FCSTD DOCUMENT  (FreeCAD 0.18R16146 (Git))
Label: ion
License: All rights reserved
LicenseURL: http://en.wikipedia.org/wiki/All_rights_reserved
objects: Part::Feature×332, Part::Part2DObjectPython×219, App::DocumentObjectGroup×23
note: 551 computed .brp shape members not serialized (recipe doc carries the construction recipe); baked Part::Feature solids carry a one-line shape summary decoded from their .brp

FEATURE [Part::Part2DObjectPython] Line030  # Draft 2D object (typed FeaturePython)
  ChamferSize = 0
  Closed = false
  End = (163,-79,0)
  FilletRadius = 0
  Length = 76
  MakeFace = false
  Placement = pos=(86,-79,0) rot=(0,0,1;0rad)
  Points = (2) [(1,0,0),(77,0,0)]
  Start = (87,-79,0)
  Subdivisions = 0
FEATURE [Part::Part2DObjectPython] Line038  # Draft 2D object (typed FeaturePython)
  ChamferSize = 0
  Closed = false
  End = (19.75,-79,0)
  FilletRadius = 0
  Length = 19.75
  MakeFace = false
  Placement = pos=(-4.8e-15,-79,0) rot=(0,0,1;0rad)
  Points = (2) [(4.8e-15,0,0),(19.75,0,0)]
  Start = (0,-79,0)
  Subdivisions = 0
FEATURE [Part::Part2DObjectPython] Arc  # Draft 2D object (typed FeaturePython)
  FirstAngle = 90
  LastAngle = 180
  MakeFace = false
  Placement = pos=(26.5,5,0) rot=(0,0,1;0rad)
  Radius = 1
FEATURE [Part::Part2DObjectPython] Arc001  # Draft 2D object (typed FeaturePython)
  FirstAngle = 0
  LastAngle = 90
  MakeFace = false
  Placement = pos=(32.5,5,0) rot=(0,0,1;0rad)
  Radius = 1
FEATURE [Part::Part2DObjectPython] Arc003  # Draft 2D object (typed FeaturePython)
  FirstAngle = -180
  LastAngle = -90
  MakeFace = false
  Placement = pos=(34.5,2,0) rot=(0,0,1;0rad)
  Radius = 1
FEATURE [Part::Part2DObjectPython] Line053  # Draft 2D object (typed FeaturePython)
  ChamferSize = 0
  Closed = false
  End = (25.5,2,0)
  FilletRadius = 0
  Length = 3
  MakeFace = false
  Placement = pos=(25.5,5,0) rot=(0,0,1;0rad)
  Points = (2) [(0,0,0),(0,-3,0)]
  Start = (25.5,5,0)
  Subdivisions = 0
FEATURE [Part::Part2DObjectPython] Line054  # Draft 2D object (typed FeaturePython)
  ChamferSize = 0
  Closed = true
  End = (32.5,6,0)
  FilletRadius = 0
  Length = 6
  MakeFace = false
  Placement = pos=(27,6,0) rot=(0,0,1;0rad)
  Points = (2) [(-0.5,-4.44089e-15,0),(5.5,-4.44089e-15,0)]
  Start = (26.5,6,0)
  Subdivisions = 0
FEATURE [Part::Part2DObjectPython] Line055  # Draft 2D object (typed FeaturePython)
  ChamferSize = 0
  Closed = false
  End = (33.5,2,0)
  FilletRadius = 0
  Length = 3
  MakeFace = false
  Placement = pos=(33.5,5,0) rot=(0,0,1;0rad)
  Points = (2) [(0,0,0),(0,-3,0)]
  Start = (33.5,5,0)
  Subdivisions = 0
FEATURE [Part::Part2DObjectPython] Arc004  # Draft 2D object (typed FeaturePython)
  FirstAngle = -90
  LastAngle = 0
  MakeFace = false
  Placement = pos=(81.75,2,0) rot=(0,0,1;0rad)
  Radius = 1
FEATURE [Part::Part2DObjectPython] Arc005  # Draft 2D object (typed FeaturePython)
  FirstAngle = -180
  LastAngle = -90
  MakeFace = false
  Placement = pos=(91.75,2,0) rot=(0,0,1;0rad)
  Radius = 1
FEATURE [Part::Part2DObjectPython] Line056  # Draft 2D object (typed FeaturePython)
  ChamferSize = 0
  Closed = false
  End = (90.75,2,0)
  FilletRadius = 0
  Length = 3
  MakeFace = false
  Placement = pos=(90.75,5,0) rot=(0,0,1;0rad)
  Points = (2) [(0,0,0),(0,-3,0)]
  Start = (90.75,5,0)
  Subdivisions = 0
FEATURE [Part::Part2DObjectPython] Arc006  # Draft 2D object (typed FeaturePython)
  FirstAngle = 0
  LastAngle = 90
  MakeFace = false
  Placement = pos=(89.75,5,0) rot=(0,0,1;0rad)
  Radius = 1
FEATURE [Part::Part2DObjectPython] Arc007  # Draft 2D object (typed FeaturePython)
  FirstAngle = 90
  LastAngle = 180
  MakeFace = false
  Placement = pos=(83.75,5,0) rot=(0,0,1;0rad)
  Radius = 1
FEATURE [Part::Part2DObjectPython] Line057  # Draft 2D object (typed FeaturePython)
  ChamferSize = 0
  Closed = false
  End = (82.75,2,0)
  FilletRadius = 0
  Length = 3
  MakeFace = false
  Placement = pos=(82.75,5,0) rot=(0,0,1;0rad)
  Points = (2) [(0,0,0),(0,-3,0)]
  Start = (82.75,5,0)
  Subdivisions = 0
FEATURE [Part::Part2DObjectPython] Line058  # Draft 2D object (typed FeaturePython)
  ChamferSize = 0
  Closed = false
  End = (89.75,6,0)
  FilletRadius = 0
  Length = 6
  MakeFace = false
  Placement = pos=(84.25,6,0) rot=(0,0,1;0rad)
  Points = (2) [(-0.5,-1.42109e-14,0),(5.5,-1.42109e-14,0)]
  Start = (83.75,6,0)
  Subdivisions = 0
FEATURE [App::DocumentObjectGroup] Group001  label="Nub2"
  Group = -> [Arc007,Arc006,Arc004,Arc005,Line057,Line058,Line056]
FEATURE [Part::Part2DObjectPython] Arc008  # Draft 2D object (typed FeaturePython)
  FirstAngle = -90
  LastAngle = 0
  MakeFace = false
  Placement = pos=(158.25,2,0) rot=(0,0,1;0rad)
  Radius = 1
FEATURE [Part::Part2DObjectPython] Arc009  # Draft 2D object (typed FeaturePython)
  FirstAngle = -180
  LastAngle = -90
  MakeFace = false
  Placement = pos=(168.25,2,0) rot=(0,0,1;0rad)
  Radius = 1
FEATURE [Part::Part2DObjectPython] Line060  # Draft 2D object (typed FeaturePython)
  ChamferSize = 0
  Closed = false
  End = (167.25,2,0)
  FilletRadius = 0
  Length = 3
  MakeFace = false
  Placement = pos=(167.25,5,0) rot=(0,0,1;0rad)
  Points = (2) [(0,0,0),(0,-3,0)]
  Start = (167.25,5,0)
  Subdivisions = 0
FEATURE [Part::Part2DObjectPython] Arc010  # Draft 2D object (typed FeaturePython)
  FirstAngle = 0
  LastAngle = 90
  MakeFace = false
  Placement = pos=(166.25,5,0) rot=(0,0,1;0rad)
  Radius = 1
FEATURE [Part::Part2DObjectPython] Arc011  # Draft 2D object (typed FeaturePython)
  FirstAngle = 90
  LastAngle = 180
  MakeFace = false
  Placement = pos=(160.25,5,0) rot=(0,0,1;0rad)
  Radius = 1
FEATURE [Part::Part2DObjectPython] Line061  # Draft 2D object (typed FeaturePython)
  ChamferSize = 0
  Closed = false
  End = (159.25,2,0)
  FilletRadius = 0
  Length = 3
  MakeFace = false
  Placement = pos=(159.25,5,0) rot=(0,0,1;0rad)
  Points = (2) [(0,0,0),(0,-3,0)]
  Start = (159.25,5,0)
  Subdivisions = 0
FEATURE [Part::Part2DObjectPython] Line062  # Draft 2D object (typed FeaturePython)
  ChamferSize = 0
  Closed = false
  End = (166.25,6,0)
  FilletRadius = 0
  Length = 6
  MakeFace = false
  Placement = pos=(160.75,6,0) rot=(0,0,1;0rad)
  Points = (2) [(-0.5,-5.32907e-15,0),(5.5,-5.32907e-15,0)]
  Start = (160.25,6,0)
  Subdivisions = 0
FEATURE [App::DocumentObjectGroup] Group002  label="Nub3"
  Group = -> [Arc011,Arc010,Arc008,Arc009,Line061,Line062,Line060]
FEATURE [Part::Part2DObjectPython] Arc012  # Draft 2D object (typed FeaturePython)
  FirstAngle = 90
  LastAngle = 180
  MakeFace = false
  Placement = pos=(217.5,5,0) rot=(0,0,1;0rad)
  Radius = 1
FEATURE [Part::Part2DObjectPython] Line063  # Draft 2D object (typed FeaturePython)
  ChamferSize = 0
  Closed = false
  End = (216.5,2,0)
  FilletRadius = 0
  Length = 3
  MakeFace = false
  Placement = pos=(216.5,5,0) rot=(0,0,1;0rad)
  Points = (2) [(0,0,0),(0,-3,0)]
  Start = (216.5,5,0)
  Subdivisions = 0
FEATURE [Part::Part2DObjectPython] Arc013  # Draft 2D object (typed FeaturePython)
  FirstAngle = -90
  LastAngle = 0
  MakeFace = false
  Placement = pos=(215.5,2,0) rot=(0,0,1;0rad)
  Radius = 1
FEATURE [Part::Part2DObjectPython] Arc014  # Draft 2D object (typed FeaturePython)
  FirstAngle = -180
  LastAngle = -90
  MakeFace = false
  Placement = pos=(225.5,2,0) rot=(0,0,1;0rad)
  Radius = 1
FEATURE [Part::Part2DObjectPython] Arc015  # Draft 2D object (typed FeaturePython)
  FirstAngle = 0
  LastAngle = 90
  MakeFace = false
  Placement = pos=(223.5,5,0) rot=(0,0,1;0rad)
  Radius = 1
FEATURE [Part::Part2DObjectPython] Line064  # Draft 2D object (typed FeaturePython)
  ChamferSize = 0
  Closed = false
  End = (223.5,6,0)
  FilletRadius = 0
  Length = 6
  MakeFace = false
  Placement = pos=(218,6,0) rot=(0,0,1;0rad)
  Points = (2) [(-0.5,-6.21725e-15,0),(5.5,-6.21725e-15,0)]
  Start = (217.5,6,0)
  Subdivisions = 0
FEATURE [Part::Part2DObjectPython] Line065  # Draft 2D object (typed FeaturePython)
  ChamferSize = 0
  Closed = false
  End = (224.5,2,0)
  FilletRadius = 0
  Length = 3
  MakeFace = false
  Placement = pos=(224.5,5,0) rot=(0,0,1;0rad)
  Points = (2) [(0,0,0),(0,-3,0)]
  Start = (224.5,5,0)
  Subdivisions = 0
FEATURE [App::DocumentObjectGroup] Group003  label="Nub4"
  Group = -> [Arc012,Arc015,Arc013,Arc014,Line063,Line064,Line065]
FEATURE [Part::Part2DObjectPython] Arc018  # Draft 2D object (typed FeaturePython)
  FirstAngle = 90
  LastAngle = 180
  MakeFace = false
  Placement = pos=(0,1e-16,0) rot=(0,0,1;0rad)
  Radius = 1
FEATURE [Part::Part2DObjectPython] Arc021  # Draft 2D object (typed FeaturePython)
  FirstAngle = -180
  LastAngle = -90
  MakeFace = false
  Placement = pos=(-1e-16,-78,0) rot=(0,0,1;0rad)
  Radius = 1
FEATURE [Part::Part2DObjectPython] Arc022  # Draft 2D object (typed FeaturePython)
  FirstAngle = -90
  LastAngle = 0
  MakeFace = false
  Placement = pos=(29.75,-80,0) rot=(0,0,1;3.14159rad)
  Radius = 1
FEATURE [Part::Part2DObjectPython] Arc023  # Draft 2D object (typed FeaturePython)
  FirstAngle = -180
  LastAngle = -90
  MakeFace = false
  Placement = pos=(19.75,-80,0) rot=(0,0,1;3.14159rad)
  Radius = 1
FEATURE [Part::Part2DObjectPython] Line069  # Draft 2D object (typed FeaturePython)
  ChamferSize = 0
  Closed = false
  End = (20.75,-80,0)
  FilletRadius = 0
  Length = 3
  MakeFace = false
  Placement = pos=(20.75,-83,0) rot=(0,0,1;3.14159rad)
  Points = (2) [(0,0,0),(3.55271e-15,-3,0)]
  Start = (20.75,-83,0)
  Subdivisions = 0
FEATURE [Part::Part2DObjectPython] Arc024  # Draft 2D object (typed FeaturePython)
  FirstAngle = 0
  LastAngle = 90
  MakeFace = false
  Placement = pos=(21.75,-83,0) rot=(0,0,1;3.14159rad)
  Radius = 1
FEATURE [Part::Part2DObjectPython] Arc025  # Draft 2D object (typed FeaturePython)
  FirstAngle = 90
  LastAngle = 180
  MakeFace = false
  Placement = pos=(27.75,-83,0) rot=(0,0,1;3.14159rad)
  Radius = 1
FEATURE [Part::Part2DObjectPython] Line070  # Draft 2D object (typed FeaturePython)
  ChamferSize = 0
  Closed = false
  End = (28.75,-80,0)
  FilletRadius = 0
  Length = 3
  MakeFace = false
  Placement = pos=(28.75,-83,0) rot=(0,0,1;3.14159rad)
  Points = (2) [(0,0,0),(3.55271e-15,-3,0)]
  Start = (28.75,-83,0)
  Subdivisions = 0
FEATURE [Part::Part2DObjectPython] Line071  # Draft 2D object (typed FeaturePython)
  ChamferSize = 0
  Closed = false
  End = (21.75,-84,0)
  FilletRadius = 0
  Length = 6
  MakeFace = false
  Placement = pos=(27.25,-84,0) rot=(0,0,1;3.14159rad)
  Points = (2) [(-0.5,0,0),(5.5,0,0)]
  Start = (27.75,-84,0)
  Subdivisions = 0
FEATURE [App::DocumentObjectGroup] Group004  label="Nub5"
  Group = -> [Arc025,Arc024,Arc022,Arc023,Line070,Line071,Line069]
FEATURE [Part::Part2DObjectPython] Arc026  # Draft 2D object (typed FeaturePython)
  FirstAngle = 0
  LastAngle = 90
  MakeFace = false
  Placement = pos=(79,-83,0) rot=(0,0,1;3.14159rad)
  Radius = 1
FEATURE [Part::Part2DObjectPython] Arc027  # Draft 2D object (typed FeaturePython)
  FirstAngle = -90
  LastAngle = 0
  MakeFace = false
  Placement = pos=(87,-80,0) rot=(0,0,1;3.14159rad)
  Radius = 1
FEATURE [Part::Part2DObjectPython] Line072  # Draft 2D object (typed FeaturePython)
  ChamferSize = 0
  Closed = false
  End = (78,-80,0)
  FilletRadius = 0
  Length = 3
  MakeFace = false
  Placement = pos=(78,-83,0) rot=(0,0,1;3.14159rad)
  Points = (2) [(0,0,0),(0,-3,0)]
  Start = (78,-83,0)
  Subdivisions = 0
FEATURE [Part::Part2DObjectPython] Arc028  # Draft 2D object (typed FeaturePython)
  FirstAngle = -180
  LastAngle = -90
  MakeFace = false
  Placement = pos=(77,-80,0) rot=(0,0,1;3.14159rad)
  Radius = 1
FEATURE [Part::Part2DObjectPython] Line073  # Draft 2D object (typed FeaturePython)
  ChamferSize = 0
  Closed = false
  End = (86,-80,0)
  FilletRadius = 0
  Length = 3
  MakeFace = false
  Placement = pos=(86,-83,0) rot=(0,0,1;3.14159rad)
  Points = (2) [(0,0,0),(0,-3,0)]
  Start = (86,-83,0)
  Subdivisions = 0
FEATURE [Part::Part2DObjectPython] Arc029  # Draft 2D object (typed FeaturePython)
  FirstAngle = 90
  LastAngle = 180
  MakeFace = false
  Placement = pos=(85,-83,0) rot=(0,0,1;3.14159rad)
  Radius = 1
FEATURE [Part::Part2DObjectPython] Arc030  # Draft 2D object (typed FeaturePython)
  FirstAngle = -180
  LastAngle = -90
  MakeFace = false
  Placement = pos=(163,-80,0) rot=(0,0,1;3.14159rad)
  Radius = 1
FEATURE [Part::Part2DObjectPython] Line075  # Draft 2D object (typed FeaturePython)
  ChamferSize = 0
  Closed = false
  End = (172,-80,0)
  FilletRadius = 0
  Length = 3
  MakeFace = false
  Placement = pos=(172,-83,0) rot=(0,0,1;3.14159rad)
  Points = (2) [(0,0,0),(0,-3,0)]
  Start = (172,-83,0)
  Subdivisions = 0
FEATURE [Part::Part2DObjectPython] Line076  # Draft 2D object (typed FeaturePython)
  ChamferSize = 0
  Closed = false
  End = (165,-84,0)
  FilletRadius = 0
  Length = 6
  MakeFace = false
  Placement = pos=(170.5,-84,0) rot=(0,0,1;3.14159rad)
  Points = (2) [(-0.5,1.42109e-14,0),(5.5,1.42109e-14,0)]
  Start = (171,-84,0)
  Subdivisions = 0
FEATURE [Part::Part2DObjectPython] Arc031  # Draft 2D object (typed FeaturePython)
  FirstAngle = 90
  LastAngle = 180
  MakeFace = false
  Placement = pos=(171,-83,0) rot=(0,0,1;3.14159rad)
  Radius = 1
FEATURE [Part::Part2DObjectPython] Arc032  # Draft 2D object (typed FeaturePython)
  FirstAngle = 0
  LastAngle = 90
  MakeFace = false
  Placement = pos=(165,-83,0) rot=(0,0,1;3.14159rad)
  Radius = 1
FEATURE [Part::Part2DObjectPython] Arc033  # Draft 2D object (typed FeaturePython)
  FirstAngle = -90
  LastAngle = 0
  MakeFace = false
  Placement = pos=(173,-80,0) rot=(0,0,1;3.14159rad)
  Radius = 1
FEATURE [Part::Part2DObjectPython] Line078  # Draft 2D object (typed FeaturePython)
  ChamferSize = 0
  Closed = false
  End = (220.25,-79,0)
  FilletRadius = 0
  Length = 47.25
  MakeFace = false
  Placement = pos=(172,-79,0) rot=(0,0,1;0rad)
  Points = (2) [(1,-2.84217e-14,0),(48.25,-2.84217e-14,0)]
  Start = (173,-79,0)
  Subdivisions = 0
FEATURE [Part::Part2DObjectPython] Arc034  # Draft 2D object (typed FeaturePython)
  FirstAngle = 90
  LastAngle = 180
  MakeFace = false
  Placement = pos=(228.25,-83,0) rot=(0,0,1;3.14159rad)
  Radius = 1
FEATURE [Part::Part2DObjectPython] Arc035  # Draft 2D object (typed FeaturePython)
  FirstAngle = 0
  LastAngle = 90
  MakeFace = false
  Placement = pos=(222.25,-83,0) rot=(0,0,1;3.14159rad)
  Radius = 1
FEATURE [Part::Part2DObjectPython] Arc037  # Draft 2D object (typed FeaturePython)
  FirstAngle = -90
  LastAngle = 0
  MakeFace = false
  Placement = pos=(230.25,-80,0) rot=(0,0,1;3.14159rad)
  Radius = 1
FEATURE [Part::Part2DObjectPython] Line082  # Draft 2D object (typed FeaturePython)
  ChamferSize = 0
  Closed = false
  End = (250,-79,0)
  FilletRadius = 0
  Length = 19.75
  MakeFace = false
  Placement = pos=(229,-79,0) rot=(0,0,1;0rad)
  Points = (2) [(1.25,-7.10543e-14,0),(21,-8.52651e-14,0)]
  Start = (230.25,-79,0)
  Subdivisions = 0
FEATURE [App::DocumentObjectGroup] Group008
  Group = -> [Arc018,Arc021]
FEATURE [Part::Part2DObjectPython] Arc039  # Draft 2D object (typed FeaturePython)
  FirstAngle = 90
  LastAngle = 180
  MakeFace = false
  Placement = pos=(250,-78,0) rot=(0,0,1;3.14159rad)
  Radius = 1
FEATURE [Part::Part2DObjectPython] Line084  # Draft 2D object (typed FeaturePython)
  ChamferSize = 0
  Closed = false
  End = (248.5,0,0)
  FilletRadius = 0
  Length = 247
  MakeFace = false
  Placement = pos=(1,0,0) rot=(0,0,1;0rad)
  Points = (2) [(0.5,0,0),(247.5,0,0)]
  Start = (1.5,0,0)
  Subdivisions = 0
FEATURE [Part::Part2DObjectPython] Line087  # Draft 2D object (typed FeaturePython)
  ChamferSize = 0
  Closed = false
  End = (249.5,-1,0)
  FilletRadius = 0
  Length = 76
  MakeFace = false
  Placement = pos=(249.5,-77.5,0) rot=(0,0,1;0rad)
  Points = (2) [(0,0.5,0),(0,76.5,0)]
  Start = (249.5,-77,0)
  Subdivisions = 0
FEATURE [Part::Part2DObjectPython] Arc040  # Draft 2D object (typed FeaturePython)
  FirstAngle = 90
  LastAngle = 180
  MakeFace = false
  Placement = pos=(1.5,-1,0) rot=(0,0,1;0rad)
  Radius = 1
FEATURE [Part::Part2DObjectPython] Arc041  # Draft 2D object (typed FeaturePython)
  FirstAngle = -180
  LastAngle = -90
  MakeFace = false
  Placement = pos=(1.5,-77,0) rot=(0,0,1;0rad)
  Radius = 1
FEATURE [Part::Part2DObjectPython] Arc042  # Draft 2D object (typed FeaturePython)
  FirstAngle = 90
  LastAngle = 180
  MakeFace = false
  Placement = pos=(248.5,-77,0) rot=(0,0,1;3.14159rad)
  Radius = 1
FEATURE [Part::Part2DObjectPython] Arc043  # Draft 2D object (typed FeaturePython)
  FirstAngle = -180
  LastAngle = -90
  MakeFace = false
  Placement = pos=(248.5,-1,0) rot=(0,0,1;3.14159rad)
  Radius = 1
FEATURE [Part::Feature] Shape004
  Placement = pos=(1.07996,-77.3576,0) rot=(0,0,1;0rad)
  shape: bbox 2e-07 x 4.701 x 2e-07 mm, 0 faces, 0 solids (baked)
FEATURE [Part::Feature] Shape005
  Placement = pos=(1.07996,-77.3576,0) rot=(0,0,1;0rad)
  shape: bbox 1.525 x 2e-07 x 2e-07 mm, 0 faces, 0 solids (baked)
FEATURE [Part::Feature] Shape006
  Placement = pos=(1.07996,-77.3576,0) rot=(0,0,1;0rad)
  shape: bbox 2e-07 x 3.23 x 2e-07 mm, 0 faces, 0 solids (baked)
FEATURE [Part::Feature] Shape007
  Placement = pos=(1.07996,-77.3576,0) rot=(0,0,1;0rad)
  shape: bbox 1.726 x 2e-07 x 2e-07 mm, 0 faces, 0 solids (baked)
FEATURE [Part::Feature] Shape008
  Placement = pos=(1.07996,-77.3576,0) rot=(0,0,1;0rad)
  shape: bbox 2e-07 x 0.9219 x 2e-07 mm, 0 faces, 0 solids (baked)
FEATURE [Part::Feature] Shape009
  Placement = pos=(1.07996,-77.3576,0) rot=(0,0,1;0rad)
  shape: bbox 3.299 x 2e-07 x 2e-07 mm, 0 faces, 0 solids (baked)
FEATURE [Part::Feature] Shape010
  Placement = pos=(1.07996,-77.3576,0) rot=(0,0,1;0rad)
  shape: bbox 2e-07 x 0.9219 x 2e-07 mm, 0 faces, 0 solids (baked)
FEATURE [Part::Feature] Shape011
  Placement = pos=(1.07996,-77.3576,0) rot=(0,0,1;0rad)
  shape: bbox 1.725 x 2e-07 x 2e-07 mm, 0 faces, 0 solids (baked)
FEATURE [Part::Feature] Shape012
  Placement = pos=(1.07996,-77.3576,0) rot=(0,0,1;0rad)
  shape: bbox 2e-07 x 3.23 x 2e-07 mm, 0 faces, 0 solids (baked)
FEATURE [Part::Feature] Shape013
  Placement = pos=(1.07996,-77.3576,0) rot=(0,0,1;0rad)
  shape: bbox 0.826 x 2e-07 x 2e-07 mm, 0 faces, 0 solids (baked)
FEATURE [Part::Feature] Shape014
  Placement = pos=(1.07996,-77.3576,0) rot=(0,0,1;0rad)
  shape: bbox 2e-07 x 2.799 x 2e-07 mm, 0 faces, 0 solids (baked)
FEATURE [Part::Feature] Shape015
  Placement = pos=(1.07996,-77.3576,0) rot=(0,0,1;0rad)
  shape: bbox 0.826 x 2e-07 x 2e-07 mm, 0 faces, 0 solids (baked)
FEATURE [Part::Feature] Shape016
  Placement = pos=(1.07996,-77.3576,0) rot=(0,0,1;0rad)
  shape: bbox 2e-07 x 6.27 x 2e-07 mm, 0 faces, 0 solids (baked)
FEATURE [Part::Feature] Shape017
  Placement = pos=(1.07996,-77.3576,0) rot=(0,0,1;0rad)
  shape: bbox 1.725 x 2e-07 x 2e-07 mm, 0 faces, 0 solids (baked)
FEATURE [Part::Feature] Shape018
  Placement = pos=(1.07996,-77.3576,0) rot=(0,0,1;0rad)
  shape: bbox 2e-07 x 0.9812 x 2e-07 mm, 0 faces, 0 solids (baked)
FEATURE [Part::Feature] Shape019
  Placement = pos=(1.07996,-77.3576,0) rot=(0,0,1;0rad)
  shape: bbox 3.299 x 2e-07 x 2e-07 mm, 0 faces, 0 solids (baked)
FEATURE [Part::Feature] Shape020
  Placement = pos=(1.07996,-77.3576,0) rot=(0,0,1;0rad)
  shape: bbox 2e-07 x 0.9812 x 2e-07 mm, 0 faces, 0 solids (baked)
FEATURE [Part::Feature] Shape021
  Placement = pos=(1.07996,-77.3576,0) rot=(0,0,1;0rad)
  shape: bbox 1.726 x 2e-07 x 2e-07 mm, 0 faces, 0 solids (baked)
FEATURE [Part::Feature] Shape022
  Placement = pos=(1.07996,-77.3576,0) rot=(0,0,1;0rad)
  shape: bbox 2e-07 x 4.469 x 2e-07 mm, 0 faces, 0 solids (baked)
FEATURE [Part::Feature] Shape023
  Placement = pos=(1.07996,-77.3576,0) rot=(0,0,1;0rad)
  shape: bbox 1.525 x 2e-07 x 2e-07 mm, 0 faces, 0 solids (baked)
FEATURE [Part::Feature] Shape024
  Placement = pos=(1.07996,-77.3576,0) rot=(0,0,1;0rad)
  shape: bbox 2e-07 x 4.699 x 2e-07 mm, 0 faces, 0 solids (baked)
FEATURE [Part::Feature] Shape025
  Placement = pos=(1.07996,-77.3576,0) rot=(0,0,1;0rad)
  shape: bbox 14 x 2e-07 x 2e-07 mm, 0 faces, 0 solids (baked)
FEATURE [Part::Feature] Shape026
  Placement = pos=(1.07996,-77.3576,0) rot=(0,0,1;0rad)
  shape: bbox 2e-07 x 4.699 x 2e-07 mm, 0 faces, 0 solids (baked)
FEATURE [Part::Feature] Shape027
  Placement = pos=(1.07996,-77.3576,0) rot=(0,0,1;0rad)
  shape: bbox 1.526 x 2e-07 x 2e-07 mm, 0 faces, 0 solids (baked)
FEATURE [Part::Feature] Shape028
  Placement = pos=(1.07996,-77.3576,0) rot=(0,0,1;0rad)
  shape: bbox 2e-07 x 4.469 x 2e-07 mm, 0 faces, 0 solids (baked)
FEATURE [Part::Feature] Shape029
  Placement = pos=(1.07996,-77.3576,0) rot=(0,0,1;0rad)
  shape: bbox 1.725 x 2e-07 x 2e-07 mm, 0 faces, 0 solids (baked)
FEATURE [Part::Feature] Shape030
  Placement = pos=(1.07996,-77.3576,0) rot=(0,0,1;0rad)
  shape: bbox 2e-07 x 0.9812 x 2e-07 mm, 0 faces, 0 solids (baked)
FEATURE [Part::Feature] Shape031
  Placement = pos=(1.07996,-77.3576,0) rot=(0,0,1;0rad)
  shape: bbox 3.299 x 2e-07 x 2e-07 mm, 0 faces, 0 solids (baked)
FEATURE [Part::Feature] Shape032
  Placement = pos=(1.07996,-77.3576,0) rot=(0,0,1;0rad)
  shape: bbox 2e-07 x 0.9812 x 2e-07 mm, 0 faces, 0 solids (baked)
FEATURE [Part::Feature] Shape033
  Placement = pos=(1.07996,-77.3576,0) rot=(0,0,1;0rad)
  shape: bbox 1.725 x 2e-07 x 2e-07 mm, 0 faces, 0 solids (baked)
FEATURE [Part::Feature] Shape034
  Placement = pos=(1.07996,-77.3576,0) rot=(0,0,1;0rad)
  shape: bbox 2e-07 x 6.27 x 2e-07 mm, 0 faces, 0 solids (baked)
FEATURE [Part::Feature] Shape035
  Placement = pos=(1.07996,-77.3576,0) rot=(0,0,1;0rad)
  shape: bbox 0.826 x 2e-07 x 2e-07 mm, 0 faces, 0 solids (baked)
FEATURE [Part::Feature] Shape036
  Placement = pos=(1.07996,-77.3576,0) rot=(0,0,1;0rad)
  shape: bbox 2e-07 x 2.799 x 2e-07 mm, 0 faces, 0 solids (baked)
FEATURE [Part::Feature] Shape037
  Placement = pos=(1.07996,-77.3576,0) rot=(0,0,1;0rad)
  shape: bbox 0.826 x 2e-07 x 2e-07 mm, 0 faces, 0 solids (baked)
FEATURE [Part::Feature] Shape038
  Placement = pos=(1.07996,-77.3576,0) rot=(0,0,1;0rad)
  shape: bbox 2e-07 x 3.23 x 2e-07 mm, 0 faces, 0 solids (baked)
FEATURE [Part::Feature] Shape039
  Placement = pos=(1.07996,-77.3576,0) rot=(0,0,1;0rad)
  shape: bbox 1.725 x 2e-07 x 2e-07 mm, 0 faces, 0 solids (baked)
FEATURE [Part::Feature] Shape040
  Placement = pos=(1.07996,-77.3576,0) rot=(0,0,1;0rad)
  shape: bbox 2e-07 x 0.9219 x 2e-07 mm, 0 faces, 0 solids (baked)
FEATURE [Part::Feature] Shape041
  Placement = pos=(1.07996,-77.3576,0) rot=(0,0,1;0rad)
  shape: bbox 3.299 x 2e-07 x 2e-07 mm, 0 faces, 0 solids (baked)
FEATURE [Part::Feature] Shape042
  Placement = pos=(1.07996,-77.3576,0) rot=(0,0,1;0rad)
  shape: bbox 2e-07 x 0.9219 x 2e-07 mm, 0 faces, 0 solids (baked)
FEATURE [Part::Feature] Shape043
  Placement = pos=(1.07996,-77.3576,0) rot=(0,0,1;0rad)
  shape: bbox 1.725 x 2e-07 x 2e-07 mm, 0 faces, 0 solids (baked)
FEATURE [Part::Feature] Shape044
  Placement = pos=(1.07996,-77.3576,0) rot=(0,0,1;0rad)
  shape: bbox 2e-07 x 3.23 x 2e-07 mm, 0 faces, 0 solids (baked)
FEATURE [Part::Feature] Shape045
  Placement = pos=(1.07996,-77.3576,0) rot=(0,0,1;0rad)
  shape: bbox 1.526 x 2e-07 x 2e-07 mm, 0 faces, 0 solids (baked)
FEATURE [Part::Feature] Shape046
  Placement = pos=(1.07996,-77.3576,0) rot=(0,0,1;0rad)
  shape: bbox 2e-07 x 4.701 x 2e-07 mm, 0 faces, 0 solids (baked)
FEATURE [Part::Feature] Shape047
  Placement = pos=(1.07996,-77.3576,0) rot=(0,0,1;0rad)
  shape: bbox 14 x 2e-07 x 2e-07 mm, 0 faces, 0 solids (baked)
FEATURE [Part::Feature] Shape048
  Placement = pos=(1.07996,-77.3576,0) rot=(0,0,1;0rad)
  shape: bbox 2e-07 x 4.701 x 2e-07 mm, 0 faces, 0 solids (baked)
FEATURE [Part::Feature] Shape049
  Placement = pos=(1.07996,-77.3576,0) rot=(0,0,1;0rad)
  shape: bbox 1.525 x 2e-07 x 2e-07 mm, 0 faces, 0 solids (baked)
FEATURE [Part::Feature] Shape050
  Placement = pos=(1.07996,-77.3576,0) rot=(0,0,1;0rad)
  shape: bbox 2e-07 x 3.23 x 2e-07 mm, 0 faces, 0 solids (baked)
FEATURE [Part::Feature] Shape051
  Placement = pos=(1.07996,-77.3576,0) rot=(0,0,1;0rad)
  shape: bbox 1.726 x 2e-07 x 2e-07 mm, 0 faces, 0 solids (baked)
FEATURE [Part::Feature] Shape052
  Placement = pos=(1.07996,-77.3576,0) rot=(0,0,1;0rad)
  shape: bbox 2e-07 x 0.9219 x 2e-07 mm, 0 faces, 0 solids (baked)
FEATURE [Part::Feature] Shape053
  Placement = pos=(1.07996,-77.3576,0) rot=(0,0,1;0rad)
  shape: bbox 3.299 x 2e-07 x 2e-07 mm, 0 faces, 0 solids (baked)
FEATURE [Part::Feature] Shape054
  Placement = pos=(1.07996,-77.3576,0) rot=(0,0,1;0rad)
  shape: bbox 2e-07 x 0.9219 x 2e-07 mm, 0 faces, 0 solids (baked)
FEATURE [Part::Feature] Shape055
  Placement = pos=(1.07996,-77.3576,0) rot=(0,0,1;0rad)
  shape: bbox 1.725 x 2e-07 x 2e-07 mm, 0 faces, 0 solids (baked)
FEATURE [Part::Feature] Shape056
  Placement = pos=(1.07996,-77.3576,0) rot=(0,0,1;0rad)
  shape: bbox 2e-07 x 3.23 x 2e-07 mm, 0 faces, 0 solids (baked)
FEATURE [Part::Feature] Shape057
  Placement = pos=(1.07996,-77.3576,0) rot=(0,0,1;0rad)
  shape: bbox 0.8255 x 2e-07 x 2e-07 mm, 0 faces, 0 solids (baked)
FEATURE [Part::Feature] Shape058
  Placement = pos=(1.07996,-77.3576,0) rot=(0,0,1;0rad)
  shape: bbox 2e-07 x 2.799 x 2e-07 mm, 0 faces, 0 solids (baked)
FEATURE [Part::Feature] Shape059
  Placement = pos=(1.07996,-77.3576,0) rot=(0,0,1;0rad)
  shape: bbox 0.8255 x 2e-07 x 2e-07 mm, 0 faces, 0 solids (baked)
FEATURE [Part::Feature] Shape060
  Placement = pos=(1.07996,-77.3576,0) rot=(0,0,1;0rad)
  shape: bbox 2e-07 x 6.27 x 2e-07 mm, 0 faces, 0 solids (baked)
FEATURE [Part::Feature] Shape061
  Placement = pos=(1.07996,-77.3576,0) rot=(0,0,1;0rad)
  shape: bbox 1.725 x 2e-07 x 2e-07 mm, 0 faces, 0 solids (baked)
FEATURE [Part::Feature] Shape062
  Placement = pos=(1.07996,-77.3576,0) rot=(0,0,1;0rad)
  shape: bbox 2e-07 x 0.9812 x 2e-07 mm, 0 faces, 0 solids (baked)
FEATURE [Part::Feature] Shape063
  Placement = pos=(1.07996,-77.3576,0) rot=(0,0,1;0rad)
  shape: bbox 3.299 x 2e-07 x 2e-07 mm, 0 faces, 0 solids (baked)
FEATURE [Part::Feature] Shape064
  Placement = pos=(1.07996,-77.3576,0) rot=(0,0,1;0rad)
  shape: bbox 2e-07 x 0.9812 x 2e-07 mm, 0 faces, 0 solids (baked)
FEATURE [Part::Feature] Shape065
  Placement = pos=(1.07996,-77.3576,0) rot=(0,0,1;0rad)
  shape: bbox 1.726 x 2e-07 x 2e-07 mm, 0 faces, 0 solids (baked)
FEATURE [Part::Feature] Shape066
  Placement = pos=(1.07996,-77.3576,0) rot=(0,0,1;0rad)
  shape: bbox 2e-07 x 4.469 x 2e-07 mm, 0 faces, 0 solids (baked)
FEATURE [Part::Feature] Shape067
  Placement = pos=(1.07996,-77.3576,0) rot=(0,0,1;0rad)
  shape: bbox 1.525 x 2e-07 x 2e-07 mm, 0 faces, 0 solids (baked)
FEATURE [Part::Feature] Shape068
  Placement = pos=(1.07996,-77.3576,0) rot=(0,0,1;0rad)
  shape: bbox 2e-07 x 4.699 x 2e-07 mm, 0 faces, 0 solids (baked)
FEATURE [Part::Feature] Shape069
  Placement = pos=(1.07996,-77.3576,0) rot=(0,0,1;0rad)
  shape: bbox 14 x 2e-07 x 2e-07 mm, 0 faces, 0 solids (baked)
FEATURE [Part::Feature] Shape070
  Placement = pos=(1.07996,-77.3576,0) rot=(0,0,1;0rad)
  shape: bbox 2e-07 x 4.699 x 2e-07 mm, 0 faces, 0 solids (baked)
FEATURE [Part::Feature] Shape071
  Placement = pos=(1.07996,-77.3576,0) rot=(0,0,1;0rad)
  shape: bbox 1.526 x 2e-07 x 2e-07 mm, 0 faces, 0 solids (baked)
FEATURE [Part::Feature] Shape072
  Placement = pos=(1.07996,-77.3576,0) rot=(0,0,1;0rad)
  shape: bbox 2e-07 x 4.469 x 2e-07 mm, 0 faces, 0 solids (baked)
FEATURE [Part::Feature] Shape073
  Placement = pos=(1.07996,-77.3576,0) rot=(0,0,1;0rad)
  shape: bbox 1.724 x 2e-07 x 2e-07 mm, 0 faces, 0 solids (baked)
FEATURE [Part::Feature] Shape074
  Placement = pos=(1.07996,-77.3576,0) rot=(0,0,1;0rad)
  shape: bbox 2e-07 x 0.9812 x 2e-07 mm, 0 faces, 0 solids (baked)
FEATURE [Part::Feature] Shape075
  Placement = pos=(1.07996,-77.3576,0) rot=(0,0,1;0rad)
  shape: bbox 3.3 x 2e-07 x 2e-07 mm, 0 faces, 0 solids (baked)
FEATURE [Part::Feature] Shape076
  Placement = pos=(1.07996,-77.3576,0) rot=(0,0,1;0rad)
  shape: bbox 2e-07 x 0.9812 x 2e-07 mm, 0 faces, 0 solids (baked)
FEATURE [Part::Feature] Shape077
  Placement = pos=(1.07996,-77.3576,0) rot=(0,0,1;0rad)
  shape: bbox 1.725 x 2e-07 x 2e-07 mm, 0 faces, 0 solids (baked)
FEATURE [Part::Feature] Shape078
  Placement = pos=(1.07996,-77.3576,0) rot=(0,0,1;0rad)
  shape: bbox 2e-07 x 6.27 x 2e-07 mm, 0 faces, 0 solids (baked)
FEATURE [Part::Feature] Shape079
  Placement = pos=(1.07996,-77.3576,0) rot=(0,0,1;0rad)
  shape: bbox 0.826 x 2e-07 x 2e-07 mm, 0 faces, 0 solids (baked)
FEATURE [Part::Feature] Shape080
  Placement = pos=(1.07996,-77.3576,0) rot=(0,0,1;0rad)
  shape: bbox 2e-07 x 2.799 x 2e-07 mm, 0 faces, 0 solids (baked)
FEATURE [Part::Feature] Shape081
  Placement = pos=(1.07996,-77.3576,0) rot=(0,0,1;0rad)
  shape: bbox 0.826 x 2e-07 x 2e-07 mm, 0 faces, 0 solids (baked)
FEATURE [Part::Feature] Shape082
  Placement = pos=(1.07996,-77.3576,0) rot=(0,0,1;0rad)
  shape: bbox 2e-07 x 3.23 x 2e-07 mm, 0 faces, 0 solids (baked)
FEATURE [Part::Feature] Shape083
  Placement = pos=(1.07996,-77.3576,0) rot=(0,0,1;0rad)
  shape: bbox 1.725 x 2e-07 x 2e-07 mm, 0 faces, 0 solids (baked)
FEATURE [Part::Feature] Shape084
  Placement = pos=(1.07996,-77.3576,0) rot=(0,0,1;0rad)
  shape: bbox 2e-07 x 0.9219 x 2e-07 mm, 0 faces, 0 solids (baked)
FEATURE [Part::Feature] Shape085
  Placement = pos=(1.07996,-77.3576,0) rot=(0,0,1;0rad)
  shape: bbox 3.3 x 2e-07 x 2e-07 mm, 0 faces, 0 solids (baked)
FEATURE [Part::Feature] Shape086
  Placement = pos=(1.07996,-77.3576,0) rot=(0,0,1;0rad)
  shape: bbox 2e-07 x 0.9219 x 2e-07 mm, 0 faces, 0 solids (baked)
FEATURE [Part::Feature] Shape087
  Placement = pos=(1.07996,-77.3576,0) rot=(0,0,1;0rad)
  shape: bbox 1.724 x 2e-07 x 2e-07 mm, 0 faces, 0 solids (baked)
FEATURE [Part::Feature] Shape088
  Placement = pos=(1.07996,-77.3576,0) rot=(0,0,1;0rad)
  shape: bbox 2e-07 x 3.23 x 2e-07 mm, 0 faces, 0 solids (baked)
FEATURE [Part::Feature] Shape089
  Placement = pos=(1.07996,-77.3576,0) rot=(0,0,1;0rad)
  shape: bbox 1.526 x 2e-07 x 2e-07 mm, 0 faces, 0 solids (baked)
FEATURE [Part::Feature] Shape090
  Placement = pos=(1.07996,-77.3576,0) rot=(0,0,1;0rad)
  shape: bbox 2e-07 x 4.701 x 2e-07 mm, 0 faces, 0 solids (baked)
FEATURE [Part::Feature] Shape091
  Placement = pos=(1.07996,-77.3576,0) rot=(0,0,1;0rad)
  shape: bbox 14 x 2e-07 x 2e-07 mm, 0 faces, 0 solids (baked)
FEATURE [Part::Feature] Shape092
  Placement = pos=(1.07996,-77.3576,0) rot=(0,0,1;0rad)
  shape: bbox 14 x 2e-07 x 2e-07 mm, 0 faces, 0 solids (baked)
FEATURE [Part::Feature] Shape093
  Placement = pos=(1.07996,-77.3576,0) rot=(0,0,1;0rad)
  shape: bbox 2e-07 x 14 x 2e-07 mm, 0 faces, 0 solids (baked)
FEATURE [Part::Feature] Shape094
  Placement = pos=(1.07996,-77.3576,0) rot=(0,0,1;0rad)
  shape: bbox 14 x 2e-07 x 2e-07 mm, 0 faces, 0 solids (baked)
FEATURE [Part::Feature] Shape095
  Placement = pos=(1.07996,-77.3576,0) rot=(0,0,1;0rad)
  shape: bbox 2e-07 x 14 x 2e-07 mm, 0 faces, 0 solids (baked)
FEATURE [Part::Feature] Shape096
  Placement = pos=(1.07996,-77.3576,0) rot=(0,0,1;0rad)
  shape: bbox 14 x 2e-07 x 2e-07 mm, 0 faces, 0 solids (baked)
FEATURE [Part::Feature] Shape097
  Placement = pos=(1.07996,-77.3576,0) rot=(0,0,1;0rad)
  shape: bbox 2e-07 x 14 x 2e-07 mm, 0 faces, 0 solids (baked)
FEATURE [Part::Feature] Shape098
  Placement = pos=(1.07996,-77.3576,0) rot=(0,0,1;0rad)
  shape: bbox 14 x 2e-07 x 2e-07 mm, 0 faces, 0 solids (baked)
FEATURE [Part::Feature] Shape099
  Placement = pos=(1.07996,-77.3576,0) rot=(0,0,1;0rad)
  shape: bbox 2e-07 x 14 x 2e-07 mm, 0 faces, 0 solids (baked)
FEATURE [Part::Feature] Shape100
  Placement = pos=(1.07996,-77.3576,0) rot=(0,0,1;0rad)
  shape: bbox 14 x 2e-07 x 2e-07 mm, 0 faces, 0 solids (baked)
FEATURE [Part::Feature] Shape101
  Placement = pos=(1.07996,-77.3576,0) rot=(0,0,1;0rad)
  shape: bbox 2e-07 x 14 x 2e-07 mm, 0 faces, 0 solids (baked)
FEATURE [Part::Feature] Shape102
  Placement = pos=(1.07996,-77.3576,0) rot=(0,0,1;0rad)
  shape: bbox 14 x 2e-07 x 2e-07 mm, 0 faces, 0 solids (baked)
FEATURE [Part::Feature] Shape103
  Placement = pos=(1.07996,-77.3576,0) rot=(0,0,1;0rad)
  shape: bbox 2e-07 x 14 x 2e-07 mm, 0 faces, 0 solids (baked)
FEATURE [Part::Feature] Shape104
  Placement = pos=(1.07996,-77.3576,0) rot=(0,0,1;0rad)
  shape: bbox 14 x 2e-07 x 2e-07 mm, 0 faces, 0 solids (baked)
FEATURE [Part::Feature] Shape105
  Placement = pos=(1.07996,-77.3576,0) rot=(0,0,1;0rad)
  shape: bbox 2e-07 x 14 x 2e-07 mm, 0 faces, 0 solids (baked)
FEATURE [Part::Feature] Shape106
  Placement = pos=(1.07996,-77.3576,0) rot=(0,0,1;0rad)
  shape: bbox 14 x 2e-07 x 2e-07 mm, 0 faces, 0 solids (baked)
FEATURE [Part::Feature] Shape107
  Placement = pos=(1.07996,-77.3576,0) rot=(0,0,1;0rad)
  shape: bbox 2e-07 x 14 x 2e-07 mm, 0 faces, 0 solids (baked)
FEATURE [Part::Feature] Shape108
  Placement = pos=(1.07996,-77.3576,0) rot=(0,0,1;0rad)
  shape: bbox 14 x 2e-07 x 2e-07 mm, 0 faces, 0 solids (baked)
FEATURE [Part::Feature] Shape109
  Placement = pos=(1.07996,-77.3576,0) rot=(0,0,1;0rad)
  shape: bbox 2e-07 x 14 x 2e-07 mm, 0 faces, 0 solids (baked)
FEATURE [Part::Feature] Shape110
  Placement = pos=(1.07996,-77.3576,0) rot=(0,0,1;0rad)
  shape: bbox 14 x 2e-07 x 2e-07 mm, 0 faces, 0 solids (baked)
FEATURE [Part::Feature] Shape111
  Placement = pos=(1.07996,-77.3576,0) rot=(0,0,1;0rad)
  shape: bbox 2e-07 x 14 x 2e-07 mm, 0 faces, 0 solids (baked)
FEATURE [Part::Feature] Shape112
  Placement = pos=(1.07996,-77.3576,0) rot=(0,0,1;0rad)
  shape: bbox 14 x 2e-07 x 2e-07 mm, 0 faces, 0 solids (baked)
FEATURE [Part::Feature] Shape113
  Placement = pos=(1.07996,-77.3576,0) rot=(0,0,1;0rad)
  shape: bbox 2e-07 x 14 x 2e-07 mm, 0 faces, 0 solids (baked)
FEATURE [Part::Feature] Shape114
  Placement = pos=(1.07996,-77.3576,0) rot=(0,0,1;0rad)
  shape: bbox 14 x 2e-07 x 2e-07 mm, 0 faces, 0 solids (baked)
FEATURE [Part::Feature] Shape115
  Placement = pos=(1.07996,-77.3576,0) rot=(0,0,1;0rad)
  shape: bbox 2e-07 x 14 x 2e-07 mm, 0 faces, 0 solids (baked)
FEATURE [Part::Feature] Shape116
  Placement = pos=(1.07996,-77.3576,0) rot=(0,0,1;0rad)
  shape: bbox 14 x 2e-07 x 2e-07 mm, 0 faces, 0 solids (baked)
FEATURE [Part::Feature] Shape117
  Placement = pos=(1.07996,-77.3576,0) rot=(0,0,1;0rad)
  shape: bbox 2e-07 x 14 x 2e-07 mm, 0 faces, 0 solids (baked)
FEATURE [Part::Feature] Shape118
  Placement = pos=(1.07996,-77.3576,0) rot=(0,0,1;0rad)
  shape: bbox 14 x 2e-07 x 2e-07 mm, 0 faces, 0 solids (baked)
FEATURE [Part::Feature] Shape119
  Placement = pos=(1.07996,-77.3576,0) rot=(0,0,1;0rad)
  shape: bbox 2e-07 x 14 x 2e-07 mm, 0 faces, 0 solids (baked)
FEATURE [Part::Feature] Shape164
  Placement = pos=(1.07996,-77.3576,0) rot=(0,0,1;0rad)
  shape: bbox 14 x 2e-07 x 2e-07 mm, 0 faces, 0 solids (baked)
FEATURE [Part::Feature] Shape165
  Placement = pos=(1.07996,-77.3576,0) rot=(0,0,1;0rad)
  shape: bbox 2e-07 x 14 x 2e-07 mm, 0 faces, 0 solids (baked)
FEATURE [Part::Feature] Shape166
  Placement = pos=(1.07996,-77.3576,0) rot=(0,0,1;0rad)
  shape: bbox 14 x 2e-07 x 2e-07 mm, 0 faces, 0 solids (baked)
FEATURE [Part::Feature] Shape167
  Placement = pos=(1.07996,-77.3576,0) rot=(0,0,1;0rad)
  shape: bbox 2e-07 x 14 x 2e-07 mm, 0 faces, 0 solids (baked)
FEATURE [Part::Feature] Shape168
  Placement = pos=(1.07996,-77.3576,0) rot=(0,0,1;0rad)
  shape: bbox 14 x 2e-07 x 2e-07 mm, 0 faces, 0 solids (baked)
FEATURE [Part::Feature] Shape169
  Placement = pos=(1.07996,-77.3576,0) rot=(0,0,1;0rad)
  shape: bbox 2e-07 x 14 x 2e-07 mm, 0 faces, 0 solids (baked)
FEATURE [Part::Feature] Shape170
  Placement = pos=(1.07996,-77.3576,0) rot=(0,0,1;0rad)
  shape: bbox 14 x 2e-07 x 2e-07 mm, 0 faces, 0 solids (baked)
FEATURE [Part::Feature] Shape171
  Placement = pos=(1.07996,-77.3576,0) rot=(0,0,1;0rad)
  shape: bbox 2e-07 x 14 x 2e-07 mm, 0 faces, 0 solids (baked)
FEATURE [Part::Feature] Shape172
  Placement = pos=(1.07996,-77.3576,0) rot=(0,0,1;0rad)
  shape: bbox 14 x 2e-07 x 2e-07 mm, 0 faces, 0 solids (baked)
FEATURE [Part::Feature] Shape173
  Placement = pos=(1.07996,-77.3576,0) rot=(0,0,1;0rad)
  shape: bbox 2e-07 x 14 x 2e-07 mm, 0 faces, 0 solids (baked)
FEATURE [Part::Feature] Shape174
  Placement = pos=(1.07996,-77.3576,0) rot=(0,0,1;0rad)
  shape: bbox 14 x 2e-07 x 2e-07 mm, 0 faces, 0 solids (baked)
FEATURE [Part::Feature] Shape175
  Placement = pos=(1.07996,-77.3576,0) rot=(0,0,1;0rad)
  shape: bbox 2e-07 x 14 x 2e-07 mm, 0 faces, 0 solids (baked)
FEATURE [Part::Feature] Shape176
  Placement = pos=(1.07996,-77.3576,0) rot=(0,0,1;0rad)
  shape: bbox 14 x 2e-07 x 2e-07 mm, 0 faces, 0 solids (baked)
FEATURE [Part::Feature] Shape177
  Placement = pos=(1.07996,-77.3576,0) rot=(0,0,1;0rad)
  shape: bbox 2e-07 x 14 x 2e-07 mm, 0 faces, 0 solids (baked)
FEATURE [Part::Feature] Shape178
  Placement = pos=(1.07996,-77.3576,0) rot=(0,0,1;0rad)
  shape: bbox 14 x 2e-07 x 2e-07 mm, 0 faces, 0 solids (baked)
FEATURE [Part::Feature] Shape179
  Placement = pos=(1.07996,-77.3576,0) rot=(0,0,1;0rad)
  shape: bbox 2e-07 x 14 x 2e-07 mm, 0 faces, 0 solids (baked)
FEATURE [Part::Feature] Shape180
  Placement = pos=(1.07996,-77.3576,0) rot=(0,0,1;0rad)
  shape: bbox 14 x 2e-07 x 2e-07 mm, 0 faces, 0 solids (baked)
FEATURE [Part::Feature] Shape181
  Placement = pos=(1.07996,-77.3576,0) rot=(0,0,1;0rad)
  shape: bbox 2e-07 x 14 x 2e-07 mm, 0 faces, 0 solids (baked)
FEATURE [Part::Feature] Shape182
  Placement = pos=(1.07996,-77.3576,0) rot=(0,0,1;0rad)
  shape: bbox 14 x 2e-07 x 2e-07 mm, 0 faces, 0 solids (baked)
FEATURE [Part::Feature] Shape183
  Placement = pos=(1.07996,-77.3576,0) rot=(0,0,1;0rad)
  shape: bbox 2e-07 x 14 x 2e-07 mm, 0 faces, 0 solids (baked)
FEATURE [Part::Feature] Shape184
  Placement = pos=(1.07996,-77.3576,0) rot=(0,0,1;0rad)
  shape: bbox 14 x 2e-07 x 2e-07 mm, 0 faces, 0 solids (baked)
FEATURE [Part::Feature] Shape185
  Placement = pos=(1.07996,-77.3576,0) rot=(0,0,1;0rad)
  shape: bbox 2e-07 x 14 x 2e-07 mm, 0 faces, 0 solids (baked)
FEATURE [Part::Feature] Shape186
  Placement = pos=(1.07996,-77.3576,0) rot=(0,0,1;0rad)
  shape: bbox 14 x 2e-07 x 2e-07 mm, 0 faces, 0 solids (baked)
FEATURE [Part::Feature] Shape187
  Placement = pos=(1.07996,-77.3576,0) rot=(0,0,1;0rad)
  shape: bbox 2e-07 x 14 x 2e-07 mm, 0 faces, 0 solids (baked)
FEATURE [Part::Feature] Shape188
  Placement = pos=(1.07996,-77.3576,0) rot=(0,0,1;0rad)
  shape: bbox 14 x 2e-07 x 2e-07 mm, 0 faces, 0 solids (baked)
FEATURE [Part::Feature] Shape189
  Placement = pos=(1.07996,-77.3576,0) rot=(0,0,1;0rad)
  shape: bbox 2e-07 x 14 x 2e-07 mm, 0 faces, 0 solids (baked)
FEATURE [Part::Feature] Shape190
  Placement = pos=(1.07996,-77.3576,0) rot=(0,0,1;0rad)
  shape: bbox 14 x 2e-07 x 2e-07 mm, 0 faces, 0 solids (baked)
FEATURE [Part::Feature] Shape191
  Placement = pos=(1.07996,-77.3576,0) rot=(0,0,1;0rad)
  shape: bbox 2e-07 x 14 x 2e-07 mm, 0 faces, 0 solids (baked)
FEATURE [Part::Feature] Shape192
  Placement = pos=(1.07996,-77.3576,0) rot=(0,0,1;0rad)
  shape: bbox 14 x 2e-07 x 2e-07 mm, 0 faces, 0 solids (baked)
FEATURE [Part::Feature] Shape193
  Placement = pos=(1.07996,-77.3576,0) rot=(0,0,1;0rad)
  shape: bbox 2e-07 x 14 x 2e-07 mm, 0 faces, 0 solids (baked)
FEATURE [Part::Feature] Shape194
  Placement = pos=(1.07996,-77.3576,0) rot=(0,0,1;0rad)
  shape: bbox 14 x 2e-07 x 2e-07 mm, 0 faces, 0 solids (baked)
FEATURE [Part::Feature] Shape195
  Placement = pos=(1.07996,-77.3576,0) rot=(0,0,1;0rad)
  shape: bbox 2e-07 x 14 x 2e-07 mm, 0 faces, 0 solids (baked)
FEATURE [Part::Feature] Shape196
  Placement = pos=(1.07996,-77.3576,0) rot=(0,0,1;0rad)
  shape: bbox 14 x 2e-07 x 2e-07 mm, 0 faces, 0 solids (baked)
FEATURE [Part::Feature] Shape197
  Placement = pos=(1.07996,-77.3576,0) rot=(0,0,1;0rad)
  shape: bbox 2e-07 x 14 x 2e-07 mm, 0 faces, 0 solids (baked)
FEATURE [Part::Feature] Shape198
  Placement = pos=(1.07996,-77.3576,0) rot=(0,0,1;0rad)
  shape: bbox 14 x 2e-07 x 2e-07 mm, 0 faces, 0 solids (baked)
FEATURE [Part::Feature] Shape199
  Placement = pos=(1.07996,-77.3576,0) rot=(0,0,1;0rad)
  shape: bbox 2e-07 x 14 x 2e-07 mm, 0 faces, 0 solids (baked)
FEATURE [Part::Feature] Shape200
  Placement = pos=(1.07996,-77.3576,0) rot=(0,0,1;0rad)
  shape: bbox 14 x 2e-07 x 2e-07 mm, 0 faces, 0 solids (baked)
FEATURE [Part::Feature] Shape201
  Placement = pos=(1.07996,-77.3576,0) rot=(0,0,1;0rad)
  shape: bbox 2e-07 x 14 x 2e-07 mm, 0 faces, 0 solids (baked)
FEATURE [Part::Feature] Shape202
  Placement = pos=(1.07996,-77.3576,0) rot=(0,0,1;0rad)
  shape: bbox 14 x 2e-07 x 2e-07 mm, 0 faces, 0 solids (baked)
FEATURE [Part::Feature] Shape203
  Placement = pos=(1.07996,-77.3576,0) rot=(0,0,1;0rad)
  shape: bbox 2e-07 x 14 x 2e-07 mm, 0 faces, 0 solids (baked)
FEATURE [Part::Feature] Shape204
  Placement = pos=(1.07996,-77.3576,0) rot=(0,0,1;0rad)
  shape: bbox 2e-07 x 4.701 x 2e-07 mm, 0 faces, 0 solids (baked)
FEATURE [Part::Feature] Shape205
  Placement = pos=(1.07996,-77.3576,0) rot=(0,0,1;0rad)
  shape: bbox 1.524 x 2e-07 x 2e-07 mm, 0 faces, 0 solids (baked)
FEATURE [Part::Feature] Shape206
  Placement = pos=(1.07996,-77.3576,0) rot=(0,0,1;0rad)
  shape: bbox 2e-07 x 3.23 x 2e-07 mm, 0 faces, 0 solids (baked)
FEATURE [Part::Feature] Shape207
  Placement = pos=(1.07996,-77.3576,0) rot=(0,0,1;0rad)
  shape: bbox 1.725 x 2e-07 x 2e-07 mm, 0 faces, 0 solids (baked)
FEATURE [Part::Feature] Shape208
  Placement = pos=(1.07996,-77.3576,0) rot=(0,0,1;0rad)
  shape: bbox 2e-07 x 0.9207 x 2e-07 mm, 0 faces, 0 solids (baked)
FEATURE [Part::Feature] Shape209
  Placement = pos=(1.07996,-77.3576,0) rot=(0,0,1;0rad)
  shape: bbox 3.301 x 2e-07 x 2e-07 mm, 0 faces, 0 solids (baked)
FEATURE [Part::Feature] Shape210
  Placement = pos=(1.07996,-77.3576,0) rot=(0,0,1;0rad)
  shape: bbox 2e-07 x 0.9207 x 2e-07 mm, 0 faces, 0 solids (baked)
FEATURE [Part::Feature] Shape211
  Placement = pos=(1.07996,-77.3576,0) rot=(0,0,1;0rad)
  shape: bbox 1.725 x 2e-07 x 2e-07 mm, 0 faces, 0 solids (baked)
FEATURE [Part::Feature] Shape212
  Placement = pos=(1.07996,-77.3576,0) rot=(0,0,1;0rad)
  shape: bbox 2e-07 x 3.23 x 2e-07 mm, 0 faces, 0 solids (baked)
FEATURE [Part::Feature] Shape213
  Placement = pos=(1.07996,-77.3576,0) rot=(0,0,1;0rad)
  shape: bbox 0.824 x 2e-07 x 2e-07 mm, 0 faces, 0 solids (baked)
FEATURE [Part::Feature] Shape214
  Placement = pos=(1.07996,-77.3576,0) rot=(0,0,1;0rad)
  shape: bbox 2e-07 x 2.799 x 2e-07 mm, 0 faces, 0 solids (baked)
FEATURE [Part::Feature] Shape215
  Placement = pos=(1.07996,-77.3576,0) rot=(0,0,1;0rad)
  shape: bbox 0.824 x 2e-07 x 2e-07 mm, 0 faces, 0 solids (baked)
FEATURE [Part::Feature] Shape216
  Placement = pos=(1.07996,-77.3576,0) rot=(0,0,1;0rad)
  shape: bbox 2e-07 x 6.27 x 2e-07 mm, 0 faces, 0 solids (baked)
FEATURE [Part::Feature] Shape217
  Placement = pos=(1.07996,-77.3576,0) rot=(0,0,1;0rad)
  shape: bbox 1.725 x 2e-07 x 2e-07 mm, 0 faces, 0 solids (baked)
FEATURE [Part::Feature] Shape218
  Placement = pos=(1.07996,-77.3576,0) rot=(0,0,1;0rad)
  shape: bbox 2e-07 x 0.9811 x 2e-07 mm, 0 faces, 0 solids (baked)
FEATURE [Part::Feature] Shape219
  Placement = pos=(1.07996,-77.3576,0) rot=(0,0,1;0rad)
  shape: bbox 3.301 x 2e-07 x 2e-07 mm, 0 faces, 0 solids (baked)
FEATURE [Part::Feature] Shape220
  Placement = pos=(1.07996,-77.3576,0) rot=(0,0,1;0rad)
  shape: bbox 2e-07 x 0.9811 x 2e-07 mm, 0 faces, 0 solids (baked)
FEATURE [Part::Feature] Shape221
  Placement = pos=(1.07996,-77.3576,0) rot=(0,0,1;0rad)
  shape: bbox 1.725 x 2e-07 x 2e-07 mm, 0 faces, 0 solids (baked)
FEATURE [Part::Feature] Shape222
  Placement = pos=(1.07996,-77.3576,0) rot=(0,0,1;0rad)
  shape: bbox 2e-07 x 4.469 x 2e-07 mm, 0 faces, 0 solids (baked)
FEATURE [Part::Feature] Shape223
  Placement = pos=(1.07996,-77.3576,0) rot=(0,0,1;0rad)
  shape: bbox 1.524 x 2e-07 x 2e-07 mm, 0 faces, 0 solids (baked)
FEATURE [Part::Feature] Shape224
  Placement = pos=(1.07996,-77.3576,0) rot=(0,0,1;0rad)
  shape: bbox 2e-07 x 4.699 x 2e-07 mm, 0 faces, 0 solids (baked)
FEATURE [Part::Feature] Shape225
  Placement = pos=(1.07996,-77.3576,0) rot=(0,0,1;0rad)
  shape: bbox 14 x 2e-07 x 2e-07 mm, 0 faces, 0 solids (baked)
FEATURE [Part::Feature] Shape226
  Placement = pos=(1.07996,-77.3576,0) rot=(0,0,1;0rad)
  shape: bbox 2e-07 x 4.699 x 2e-07 mm, 0 faces, 0 solids (baked)
FEATURE [Part::Feature] Shape227
  Placement = pos=(1.07996,-77.3576,0) rot=(0,0,1;0rad)
  shape: bbox 1.524 x 2e-07 x 2e-07 mm, 0 faces, 0 solids (baked)
FEATURE [Part::Feature] Shape228
  Placement = pos=(1.07996,-77.3576,0) rot=(0,0,1;0rad)
  shape: bbox 2e-07 x 4.469 x 2e-07 mm, 0 faces, 0 solids (baked)
FEATURE [Part::Feature] Shape229
  Placement = pos=(1.07996,-77.3576,0) rot=(0,0,1;0rad)
  shape: bbox 1.725 x 2e-07 x 2e-07 mm, 0 faces, 0 solids (baked)
FEATURE [Part::Feature] Shape230
  Placement = pos=(1.07996,-77.3576,0) rot=(0,0,1;0rad)
  shape: bbox 2e-07 x 0.9811 x 2e-07 mm, 0 faces, 0 solids (baked)
FEATURE [Part::Feature] Shape231
  Placement = pos=(1.07996,-77.3576,0) rot=(0,0,1;0rad)
  shape: bbox 3.301 x 2e-07 x 2e-07 mm, 0 faces, 0 solids (baked)
FEATURE [Part::Feature] Shape232
  Placement = pos=(1.07996,-77.3576,0) rot=(0,0,1;0rad)
  shape: bbox 2e-07 x 0.9811 x 2e-07 mm, 0 faces, 0 solids (baked)
FEATURE [Part::Feature] Shape233
  Placement = pos=(1.07996,-77.3576,0) rot=(0,0,1;0rad)
  shape: bbox 1.725 x 2e-07 x 2e-07 mm, 0 faces, 0 solids (baked)
FEATURE [Part::Feature] Shape234
  Placement = pos=(1.07996,-77.3576,0) rot=(0,0,1;0rad)
  shape: bbox 2e-07 x 6.27 x 2e-07 mm, 0 faces, 0 solids (baked)
FEATURE [Part::Feature] Shape235
  Placement = pos=(1.07996,-77.3576,0) rot=(0,0,1;0rad)
  shape: bbox 0.824 x 2e-07 x 2e-07 mm, 0 faces, 0 solids (baked)
FEATURE [Part::Feature] Shape236
  Placement = pos=(1.07996,-77.3576,0) rot=(0,0,1;0rad)
  shape: bbox 2e-07 x 2.799 x 2e-07 mm, 0 faces, 0 solids (baked)
FEATURE [Part::Feature] Shape237
  Placement = pos=(1.07996,-77.3576,0) rot=(0,0,1;0rad)
  shape: bbox 0.824 x 2e-07 x 2e-07 mm, 0 faces, 0 solids (baked)
FEATURE [Part::Feature] Shape238
  Placement = pos=(1.07996,-77.3576,0) rot=(0,0,1;0rad)
  shape: bbox 2e-07 x 3.23 x 2e-07 mm, 0 faces, 0 solids (baked)
FEATURE [Part::Feature] Shape239
  Placement = pos=(1.07996,-77.3576,0) rot=(0,0,1;0rad)
  shape: bbox 1.725 x 2e-07 x 2e-07 mm, 0 faces, 0 solids (baked)
FEATURE [Part::Feature] Shape240
  Placement = pos=(1.07996,-77.3576,0) rot=(0,0,1;0rad)
  shape: bbox 2e-07 x 0.9207 x 2e-07 mm, 0 faces, 0 solids (baked)
FEATURE [Part::Feature] Shape241
  Placement = pos=(1.07996,-77.3576,0) rot=(0,0,1;0rad)
  shape: bbox 3.301 x 2e-07 x 2e-07 mm, 0 faces, 0 solids (baked)
FEATURE [Part::Feature] Shape242
  Placement = pos=(1.07996,-77.3576,0) rot=(0,0,1;0rad)
  shape: bbox 2e-07 x 0.9207 x 2e-07 mm, 0 faces, 0 solids (baked)
FEATURE [Part::Feature] Shape243
  Placement = pos=(1.07996,-77.3576,0) rot=(0,0,1;0rad)
  shape: bbox 1.725 x 2e-07 x 2e-07 mm, 0 faces, 0 solids (baked)
FEATURE [Part::Feature] Shape244
  Placement = pos=(1.07996,-77.3576,0) rot=(0,0,1;0rad)
  shape: bbox 2e-07 x 3.23 x 2e-07 mm, 0 faces, 0 solids (baked)
FEATURE [Part::Feature] Shape245
  Placement = pos=(1.07996,-77.3576,0) rot=(0,0,1;0rad)
  shape: bbox 1.524 x 2e-07 x 2e-07 mm, 0 faces, 0 solids (baked)
FEATURE [Part::Feature] Shape246
  Placement = pos=(1.07996,-77.3576,0) rot=(0,0,1;0rad)
  shape: bbox 2e-07 x 4.701 x 2e-07 mm, 0 faces, 0 solids (baked)
FEATURE [Part::Feature] Shape247
  Placement = pos=(1.07996,-77.3576,0) rot=(0,0,1;0rad)
  shape: bbox 14 x 2e-07 x 2e-07 mm, 0 faces, 0 solids (baked)
FEATURE [Part::Feature] Shape248
  Placement = pos=(1.07996,-77.3576,0) rot=(0,0,1;0rad)
  shape: bbox 14 x 2e-07 x 2e-07 mm, 0 faces, 0 solids (baked)
FEATURE [Part::Feature] Shape249
  Placement = pos=(1.07996,-77.3576,0) rot=(0,0,1;0rad)
  shape: bbox 2e-07 x 14 x 2e-07 mm, 0 faces, 0 solids (baked)
FEATURE [Part::Feature] Shape250
  Placement = pos=(1.07996,-77.3576,0) rot=(0,0,1;0rad)
  shape: bbox 14 x 2e-07 x 2e-07 mm, 0 faces, 0 solids (baked)
FEATURE [Part::Feature] Shape251
  Placement = pos=(1.07996,-77.3576,0) rot=(0,0,1;0rad)
  shape: bbox 2e-07 x 14 x 2e-07 mm, 0 faces, 0 solids (baked)
FEATURE [Part::Feature] Shape252
  Placement = pos=(1.07996,-77.3576,0) rot=(0,0,1;0rad)
  shape: bbox 14 x 2e-07 x 2e-07 mm, 0 faces, 0 solids (baked)
FEATURE [Part::Feature] Shape253
  Placement = pos=(1.07996,-77.3576,0) rot=(0,0,1;0rad)
  shape: bbox 2e-07 x 14 x 2e-07 mm, 0 faces, 0 solids (baked)
FEATURE [Part::Feature] Shape254
  Placement = pos=(1.07996,-77.3576,0) rot=(0,0,1;0rad)
  shape: bbox 14 x 2e-07 x 2e-07 mm, 0 faces, 0 solids (baked)
FEATURE [Part::Feature] Shape255
  Placement = pos=(1.07996,-77.3576,0) rot=(0,0,1;0rad)
  shape: bbox 2e-07 x 14 x 2e-07 mm, 0 faces, 0 solids (baked)
FEATURE [Part::Feature] Shape256
  Placement = pos=(1.07996,-77.3576,0) rot=(0,0,1;0rad)
  shape: bbox 14 x 2e-07 x 2e-07 mm, 0 faces, 0 solids (baked)
FEATURE [Part::Feature] Shape257
  Placement = pos=(1.07996,-77.3576,0) rot=(0,0,1;0rad)
  shape: bbox 2e-07 x 14 x 2e-07 mm, 0 faces, 0 solids (baked)
FEATURE [Part::Feature] Shape258
  Placement = pos=(1.07996,-77.3576,0) rot=(0,0,1;0rad)
  shape: bbox 14 x 2e-07 x 2e-07 mm, 0 faces, 0 solids (baked)
FEATURE [Part::Feature] Shape259
  Placement = pos=(1.07996,-77.3576,0) rot=(0,0,1;0rad)
  shape: bbox 2e-07 x 14 x 2e-07 mm, 0 faces, 0 solids (baked)
FEATURE [Part::Feature] Shape260
  Placement = pos=(1.07996,-77.3576,0) rot=(0,0,1;0rad)
  shape: bbox 14 x 2e-07 x 2e-07 mm, 0 faces, 0 solids (baked)
FEATURE [Part::Feature] Shape261
  Placement = pos=(1.07996,-77.3576,0) rot=(0,0,1;0rad)
  shape: bbox 2e-07 x 14 x 2e-07 mm, 0 faces, 0 solids (baked)
FEATURE [Part::Feature] Shape262
  Placement = pos=(1.07996,-77.3576,0) rot=(0,0,1;0rad)
  shape: bbox 14 x 2e-07 x 2e-07 mm, 0 faces, 0 solids (baked)
FEATURE [Part::Feature] Shape263
  Placement = pos=(1.07996,-77.3576,0) rot=(0,0,1;0rad)
  shape: bbox 2e-07 x 14 x 2e-07 mm, 0 faces, 0 solids (baked)
FEATURE [Part::Feature] Shape264
  Placement = pos=(1.07996,-77.3576,0) rot=(0,0,1;0rad)
  shape: bbox 14 x 2e-07 x 2e-07 mm, 0 faces, 0 solids (baked)
FEATURE [Part::Feature] Shape265
  Placement = pos=(1.07996,-77.3576,0) rot=(0,0,1;0rad)
  shape: bbox 2e-07 x 14 x 2e-07 mm, 0 faces, 0 solids (baked)
FEATURE [Part::Feature] Shape266
  Placement = pos=(1.07996,-77.3576,0) rot=(0,0,1;0rad)
  shape: bbox 14 x 2e-07 x 2e-07 mm, 0 faces, 0 solids (baked)
FEATURE [Part::Feature] Shape267
  Placement = pos=(1.07996,-77.3576,0) rot=(0,0,1;0rad)
  shape: bbox 2e-07 x 14 x 2e-07 mm, 0 faces, 0 solids (baked)
FEATURE [Part::Feature] Shape268
  Placement = pos=(1.07996,-77.3576,0) rot=(0,0,1;0rad)
  shape: bbox 14 x 2e-07 x 2e-07 mm, 0 faces, 0 solids (baked)
FEATURE [Part::Feature] Shape269
  Placement = pos=(1.07996,-77.3576,0) rot=(0,0,1;0rad)
  shape: bbox 2e-07 x 14 x 2e-07 mm, 0 faces, 0 solids (baked)
FEATURE [Part::Feature] Shape270
  Placement = pos=(1.07996,-77.3576,0) rot=(0,0,1;0rad)
  shape: bbox 14 x 2e-07 x 2e-07 mm, 0 faces, 0 solids (baked)
FEATURE [Part::Feature] Shape271
  Placement = pos=(1.07996,-77.3576,0) rot=(0,0,1;0rad)
  shape: bbox 2e-07 x 14 x 2e-07 mm, 0 faces, 0 solids (baked)
FEATURE [Part::Feature] Shape272
  Placement = pos=(1.07996,-77.3576,0) rot=(0,0,1;0rad)
  shape: bbox 14 x 2e-07 x 2e-07 mm, 0 faces, 0 solids (baked)
FEATURE [Part::Feature] Shape273
  Placement = pos=(1.07996,-77.3576,0) rot=(0,0,1;0rad)
  shape: bbox 2e-07 x 14 x 2e-07 mm, 0 faces, 0 solids (baked)
FEATURE [Part::Feature] Shape274
  Placement = pos=(1.07996,-77.3576,0) rot=(0,0,1;0rad)
  shape: bbox 14 x 2e-07 x 2e-07 mm, 0 faces, 0 solids (baked)
FEATURE [Part::Feature] Shape275
  Placement = pos=(1.07996,-77.3576,0) rot=(0,0,1;0rad)
  shape: bbox 2e-07 x 14 x 2e-07 mm, 0 faces, 0 solids (baked)
FEATURE [Part::Feature] Shape276
  Placement = pos=(1.07996,-77.3576,0) rot=(0,0,1;0rad)
  shape: bbox 14 x 2e-07 x 2e-07 mm, 0 faces, 0 solids (baked)
FEATURE [Part::Feature] Shape277
  Placement = pos=(1.07996,-77.3576,0) rot=(0,0,1;0rad)
  shape: bbox 2e-07 x 14 x 2e-07 mm, 0 faces, 0 solids (baked)
FEATURE [Part::Feature] Shape278
  Placement = pos=(1.07996,-77.3576,0) rot=(0,0,1;0rad)
  shape: bbox 14 x 2e-07 x 2e-07 mm, 0 faces, 0 solids (baked)
FEATURE [Part::Feature] Shape279
  Placement = pos=(1.07996,-77.3576,0) rot=(0,0,1;0rad)
  shape: bbox 2e-07 x 14 x 2e-07 mm, 0 faces, 0 solids (baked)
FEATURE [Part::Feature] Shape280
  Placement = pos=(1.07996,-77.3576,0) rot=(0,0,1;0rad)
  shape: bbox 14 x 2e-07 x 2e-07 mm, 0 faces, 0 solids (baked)
FEATURE [Part::Feature] Shape281
  Placement = pos=(1.07996,-77.3576,0) rot=(0,0,1;0rad)
  shape: bbox 2e-07 x 14 x 2e-07 mm, 0 faces, 0 solids (baked)
FEATURE [Part::Feature] Shape282
  Placement = pos=(1.07996,-77.3576,0) rot=(0,0,1;0rad)
  shape: bbox 14 x 2e-07 x 2e-07 mm, 0 faces, 0 solids (baked)
FEATURE [Part::Feature] Shape283
  Placement = pos=(1.07996,-77.3576,0) rot=(0,0,1;0rad)
  shape: bbox 2e-07 x 14 x 2e-07 mm, 0 faces, 0 solids (baked)
FEATURE [Part::Feature] Shape284
  Placement = pos=(1.07996,-77.3576,0) rot=(0,0,1;0rad)
  shape: bbox 14 x 2e-07 x 2e-07 mm, 0 faces, 0 solids (baked)
FEATURE [Part::Feature] Shape285
  Placement = pos=(1.07996,-77.3576,0) rot=(0,0,1;0rad)
  shape: bbox 2e-07 x 14 x 2e-07 mm, 0 faces, 0 solids (baked)
FEATURE [Part::Feature] Shape286
  Placement = pos=(1.07996,-77.3576,0) rot=(0,0,1;0rad)
  shape: bbox 14 x 2e-07 x 2e-07 mm, 0 faces, 0 solids (baked)
FEATURE [Part::Feature] Shape287
  Placement = pos=(1.07996,-77.3576,0) rot=(0,0,1;0rad)
  shape: bbox 2e-07 x 14 x 2e-07 mm, 0 faces, 0 solids (baked)
FEATURE [Part::Feature] Shape288
  Placement = pos=(1.07996,-77.3576,0) rot=(0,0,1;0rad)
  shape: bbox 14 x 2e-07 x 2e-07 mm, 0 faces, 0 solids (baked)
FEATURE [Part::Feature] Shape289
  Placement = pos=(1.07996,-77.3576,0) rot=(0,0,1;0rad)
  shape: bbox 2e-07 x 14 x 2e-07 mm, 0 faces, 0 solids (baked)
FEATURE [Part::Feature] Shape290
  Placement = pos=(1.07996,-77.3576,0) rot=(0,0,1;0rad)
  shape: bbox 14 x 2e-07 x 2e-07 mm, 0 faces, 0 solids (baked)
FEATURE [Part::Feature] Shape291
  Placement = pos=(1.07996,-77.3576,0) rot=(0,0,1;0rad)
  shape: bbox 2e-07 x 14 x 2e-07 mm, 0 faces, 0 solids (baked)
FEATURE [Part::Feature] Shape292
  Placement = pos=(1.07996,-77.3576,0) rot=(0,0,1;0rad)
  shape: bbox 14 x 2e-07 x 2e-07 mm, 0 faces, 0 solids (baked)
FEATURE [Part::Feature] Shape293
  Placement = pos=(1.07996,-77.3576,0) rot=(0,0,1;0rad)
  shape: bbox 2e-07 x 14 x 2e-07 mm, 0 faces, 0 solids (baked)
FEATURE [Part::Feature] Shape294
  Placement = pos=(1.07996,-77.3576,0) rot=(0,0,1;0rad)
  shape: bbox 14 x 2e-07 x 2e-07 mm, 0 faces, 0 solids (baked)
FEATURE [Part::Feature] Shape295
  Placement = pos=(1.07996,-77.3576,0) rot=(0,0,1;0rad)
  shape: bbox 2e-07 x 14 x 2e-07 mm, 0 faces, 0 solids (baked)
FEATURE [Part::Feature] Shape296
  Placement = pos=(1.07996,-77.3576,0) rot=(0,0,1;0rad)
  shape: bbox 14 x 2e-07 x 2e-07 mm, 0 faces, 0 solids (baked)
FEATURE [Part::Feature] Shape297
  Placement = pos=(1.07996,-77.3576,0) rot=(0,0,1;0rad)
  shape: bbox 2e-07 x 14 x 2e-07 mm, 0 faces, 0 solids (baked)
FEATURE [Part::Feature] Shape298
  Placement = pos=(1.07996,-77.3576,0) rot=(0,0,1;0rad)
  shape: bbox 14 x 2e-07 x 2e-07 mm, 0 faces, 0 solids (baked)
FEATURE [Part::Feature] Shape299
  Placement = pos=(1.07996,-77.3576,0) rot=(0,0,1;0rad)
  shape: bbox 2e-07 x 14 x 2e-07 mm, 0 faces, 0 solids (baked)
FEATURE [Part::Feature] Shape300
  Placement = pos=(1.07996,-77.3576,0) rot=(0,0,1;0rad)
  shape: bbox 14 x 2e-07 x 2e-07 mm, 0 faces, 0 solids (baked)
FEATURE [Part::Feature] Shape301
  Placement = pos=(1.07996,-77.3576,0) rot=(0,0,1;0rad)
  shape: bbox 2e-07 x 14 x 2e-07 mm, 0 faces, 0 solids (baked)
FEATURE [Part::Feature] Shape302
  Placement = pos=(1.07996,-77.3576,0) rot=(0,0,1;0rad)
  shape: bbox 14 x 2e-07 x 2e-07 mm, 0 faces, 0 solids (baked)
FEATURE [Part::Feature] Shape303
  Placement = pos=(1.07996,-77.3576,0) rot=(0,0,1;0rad)
  shape: bbox 2e-07 x 14 x 2e-07 mm, 0 faces, 0 solids (baked)
FEATURE [Part::Feature] Shape304
  Placement = pos=(1.07996,-77.3576,0) rot=(0,0,1;0rad)
  shape: bbox 14 x 2e-07 x 2e-07 mm, 0 faces, 0 solids (baked)
FEATURE [Part::Feature] Shape305
  Placement = pos=(1.07996,-77.3576,0) rot=(0,0,1;0rad)
  shape: bbox 2e-07 x 14 x 2e-07 mm, 0 faces, 0 solids (baked)
FEATURE [Part::Feature] Shape306
  Placement = pos=(1.07996,-77.3576,0) rot=(0,0,1;0rad)
  shape: bbox 14 x 2e-07 x 2e-07 mm, 0 faces, 0 solids (baked)
FEATURE [Part::Feature] Shape307
  Placement = pos=(1.07996,-77.3576,0) rot=(0,0,1;0rad)
  shape: bbox 2e-07 x 14 x 2e-07 mm, 0 faces, 0 solids (baked)
FEATURE [Part::Feature] Shape308
  Placement = pos=(1.07996,-77.3576,0) rot=(0,0,1;0rad)
  shape: bbox 14 x 2e-07 x 2e-07 mm, 0 faces, 0 solids (baked)
FEATURE [Part::Feature] Shape309
  Placement = pos=(1.07996,-77.3576,0) rot=(0,0,1;0rad)
  shape: bbox 2e-07 x 14 x 2e-07 mm, 0 faces, 0 solids (baked)
FEATURE [Part::Feature] Shape310
  Placement = pos=(1.07996,-77.3576,0) rot=(0,0,1;0rad)
  shape: bbox 14 x 2e-07 x 2e-07 mm, 0 faces, 0 solids (baked)
FEATURE [Part::Feature] Shape311
  Placement = pos=(1.07996,-77.3576,0) rot=(0,0,1;0rad)
  shape: bbox 2e-07 x 14 x 2e-07 mm, 0 faces, 0 solids (baked)
FEATURE [Part::Feature] Shape312
  Placement = pos=(1.07996,-77.3576,0) rot=(0,0,1;0rad)
  shape: bbox 14 x 2e-07 x 2e-07 mm, 0 faces, 0 solids (baked)
FEATURE [Part::Feature] Shape313
  Placement = pos=(1.07996,-77.3576,0) rot=(0,0,1;0rad)
  shape: bbox 2e-07 x 14 x 2e-07 mm, 0 faces, 0 solids (baked)
FEATURE [Part::Feature] Shape314
  Placement = pos=(1.07996,-77.3576,0) rot=(0,0,1;0rad)
  shape: bbox 14 x 2e-07 x 2e-07 mm, 0 faces, 0 solids (baked)
FEATURE [Part::Feature] Shape315
  Placement = pos=(1.07996,-77.3576,0) rot=(0,0,1;0rad)
  shape: bbox 2e-07 x 14 x 2e-07 mm, 0 faces, 0 solids (baked)
FEATURE [Part::Feature] Shape316
  Placement = pos=(1.07996,-77.3576,0) rot=(0,0,1;0rad)
  shape: bbox 14 x 2e-07 x 2e-07 mm, 0 faces, 0 solids (baked)
FEATURE [Part::Feature] Shape317
  Placement = pos=(1.07996,-77.3576,0) rot=(0,0,1;0rad)
  shape: bbox 2e-07 x 14 x 2e-07 mm, 0 faces, 0 solids (baked)
FEATURE [Part::Feature] Shape318
  Placement = pos=(1.07996,-77.3576,0) rot=(0,0,1;0rad)
  shape: bbox 14 x 2e-07 x 2e-07 mm, 0 faces, 0 solids (baked)
FEATURE [Part::Feature] Shape319
  Placement = pos=(1.07996,-77.3576,0) rot=(0,0,1;0rad)
  shape: bbox 2e-07 x 14 x 2e-07 mm, 0 faces, 0 solids (baked)
FEATURE [Part::Feature] Shape320
  Placement = pos=(1.07996,-77.3576,0) rot=(0,0,1;0rad)
  shape: bbox 14 x 2e-07 x 2e-07 mm, 0 faces, 0 solids (baked)
FEATURE [Part::Feature] Shape321
  Placement = pos=(1.07996,-77.3576,0) rot=(0,0,1;0rad)
  shape: bbox 2e-07 x 14 x 2e-07 mm, 0 faces, 0 solids (baked)
FEATURE [Part::Feature] Shape322
  Placement = pos=(1.07996,-77.3576,0) rot=(0,0,1;0rad)
  shape: bbox 14 x 2e-07 x 2e-07 mm, 0 faces, 0 solids (baked)
FEATURE [Part::Feature] Shape323
  Placement = pos=(1.07996,-77.3576,0) rot=(0,0,1;0rad)
  shape: bbox 2e-07 x 14 x 2e-07 mm, 0 faces, 0 solids (baked)
FEATURE [Part::Feature] Shape324
  Placement = pos=(1.07996,-77.3576,0) rot=(0,0,1;0rad)
  shape: bbox 14 x 2e-07 x 2e-07 mm, 0 faces, 0 solids (baked)
FEATURE [Part::Feature] Shape325
  Placement = pos=(1.07996,-77.3576,0) rot=(0,0,1;0rad)
  shape: bbox 2e-07 x 14 x 2e-07 mm, 0 faces, 0 solids (baked)
FEATURE [Part::Feature] Shape326
  Placement = pos=(1.07996,-77.3576,0) rot=(0,0,1;0rad)
  shape: bbox 14 x 2e-07 x 2e-07 mm, 0 faces, 0 solids (baked)
FEATURE [Part::Feature] Shape327
  Placement = pos=(1.07996,-77.3576,0) rot=(0,0,1;0rad)
  shape: bbox 2e-07 x 14 x 2e-07 mm, 0 faces, 0 solids (baked)
FEATURE [Part::Feature] Shape328
  Placement = pos=(1.07996,-77.3576,0) rot=(0,0,1;0rad)
  shape: bbox 14 x 2e-07 x 2e-07 mm, 0 faces, 0 solids (baked)
FEATURE [Part::Feature] Shape329
  Placement = pos=(1.07996,-77.3576,0) rot=(0,0,1;0rad)
  shape: bbox 2e-07 x 14 x 2e-07 mm, 0 faces, 0 solids (baked)
FEATURE [Part::Feature] Shape330
  Placement = pos=(1.07996,-77.3576,0) rot=(0,0,1;0rad)
  shape: bbox 14 x 2e-07 x 2e-07 mm, 0 faces, 0 solids (baked)
FEATURE [Part::Feature] Shape331
  Placement = pos=(1.07996,-77.3576,0) rot=(0,0,1;0rad)
  shape: bbox 2e-07 x 14 x 2e-07 mm, 0 faces, 0 solids (baked)
FEATURE [Part::Feature] Shape332
  Placement = pos=(1.07996,-77.3576,0) rot=(0,0,1;0rad)
  shape: bbox 14 x 2e-07 x 2e-07 mm, 0 faces, 0 solids (baked)
FEATURE [Part::Feature] Shape333
  Placement = pos=(1.07996,-77.3576,0) rot=(0,0,1;0rad)
  shape: bbox 2e-07 x 14 x 2e-07 mm, 0 faces, 0 solids (baked)
FEATURE [Part::Feature] Shape334
  Placement = pos=(1.07996,-77.3576,0) rot=(0,0,1;0rad)
  shape: bbox 14 x 2e-07 x 2e-07 mm, 0 faces, 0 solids (baked)
FEATURE [Part::Feature] Shape335
  Placement = pos=(1.07996,-77.3576,0) rot=(0,0,1;0rad)
  shape: bbox 2e-07 x 14 x 2e-07 mm, 0 faces, 0 solids (baked)
FEATURE [Part::Part2DObjectPython] Arc044  # Draft 2D object (typed FeaturePython)
  FirstAngle = -180
  LastAngle = -90
  MakeFace = false
  Placement = pos=(44.5368,-77,0) rot=(0,0,1;0rad)
  Radius = 1
FEATURE [Part::Part2DObjectPython] Arc045  # Draft 2D object (typed FeaturePython)
  FirstAngle = 90
  LastAngle = 180
  MakeFace = false
  Placement = pos=(24.4868,-77,0) rot=(0,0,1;3.14159rad)
  Radius = 1
FEATURE [Part::Part2DObjectPython] Arc046  # Draft 2D object (typed FeaturePython)
  FirstAngle = 90
  LastAngle = 180
  MakeFace = false
  Placement = pos=(205.462,-77,0) rot=(0,0,1;3.14159rad)
  Radius = 1
FEATURE [Part::Part2DObjectPython] Arc047  # Draft 2D object (typed FeaturePython)
  FirstAngle = -180
  LastAngle = -90
  MakeFace = false
  Placement = pos=(225.512,-77,0) rot=(0,0,1;0rad)
  Radius = 1
FEATURE [Part::Part2DObjectPython] Arc036  # Draft 2D object (typed FeaturePython)
  FirstAngle = -180
  LastAngle = -90
  MakeFace = false
  Placement = pos=(220.25,-80,0) rot=(0,0,1;3.14159rad)
  Radius = 1
FEATURE [Part::Part2DObjectPython] Line208  # Draft 2D object (typed FeaturePython)
  ChamferSize = 0
  Closed = false
  End = (221.25,-83,0)
  FilletRadius = 0
  Length = 3
  MakeFace = false
  Placement = pos=(221.25,-80,0) rot=(0,0,1;0rad)
  Points = (2) [(0,0,0),(0,-3,0)]
  Start = (221.25,-80,0)
  Subdivisions = 0
FEATURE [Part::Part2DObjectPython] Line209  # Draft 2D object (typed FeaturePython)
  ChamferSize = 0
  Closed = false
  End = (228.25,-84,0)
  FilletRadius = 0
  Length = 6
  MakeFace = false
  Placement = pos=(222.75,-84,0) rot=(0,0,1;0rad)
  Points = (2) [(-0.5,-7.10543e-14,0),(5.5,-7.10543e-14,0)]
  Start = (222.25,-84,0)
  Subdivisions = 0
FEATURE [Part::Part2DObjectPython] Line210  # Draft 2D object (typed FeaturePython)
  ChamferSize = 0
  Closed = false
  End = (85,-84,0)
  FilletRadius = 0
  Length = 6
  MakeFace = false
  Placement = pos=(79.5,-84,0) rot=(0,0,1;0rad)
  Points = (2) [(-0.5,0,0),(5.5,0,0)]
  Start = (79,-84,0)
  Subdivisions = 0
FEATURE [App::DocumentObjectGroup] Group005  label="Nub6"
  Group = -> [Arc029,Arc026,Arc027,Arc028,Line073,Line072,Line210]
FEATURE [Part::Part2DObjectPython] Line211  # Draft 2D object (typed FeaturePython)
  ChamferSize = 0
  Closed = false
  End = (229.25,-80,0)
  FilletRadius = 0
  Length = 3
  MakeFace = false
  Placement = pos=(229.25,-83,0) rot=(0,0,1;0rad)
  Points = (2) [(0,0,0),(0,3,0)]
  Start = (229.25,-83,0)
  Subdivisions = 0
FEATURE [App::DocumentObjectGroup] Group007  label="Nub8"
  Group = -> [Arc034,Arc035,Arc037,Arc036,Line208,Line209,Line211]
FEATURE [Part::Part2DObjectPython] Arc002  # Draft 2D object (typed FeaturePython)
  FirstAngle = -90
  LastAngle = 0
  MakeFace = false
  Placement = pos=(24.5,2,0) rot=(0,0,1;0rad)
  Radius = 1
FEATURE [App::DocumentObjectGroup] Group  label="Nub1"
  Group = -> [Arc,Arc001,Arc002,Arc003,Line053,Line054,Line055]
FEATURE [Part::Part2DObjectPython] Arc038  # Draft 2D object (typed FeaturePython)
  FirstAngle = -180
  LastAngle = -90
  MakeFace = false
  Placement = pos=(250,2.8e-14,0) rot=(0,0,1;3.14159rad)
  Radius = 1
FEATURE [App::DocumentObjectGroup] Group009
  Group = -> [Arc039,Arc038]
FEATURE [Part::Part2DObjectPython] Line  # Draft 2D object (typed FeaturePython)
  ChamferSize = 0
  Closed = false
  End = (24.5,1,0)
  FilletRadius = 0
  Length = 24.5
  MakeFace = false
  Placement = pos=(-1e-16,1,0) rot=(0,0,1;0rad)
  Points = (2) [(0,0,0),(24.5,2.61124e-15,0)]
  Start = (-1e-16,1,0)
  Subdivisions = 0
FEATURE [Part::Part2DObjectPython] Line212  # Draft 2D object (typed FeaturePython)
  ChamferSize = 0
  Closed = false
  End = (81.7,1,0)
  FilletRadius = 0
  Length = 47.2
  MakeFace = false
  Placement = pos=(34,1,0) rot=(0,0,1;0rad)
  Points = (2) [(0.5,-3.77476e-15,0),(47.7,-3.77476e-15,0)]
  Start = (34.5,1,0)
  Subdivisions = 0
FEATURE [Part::Part2DObjectPython] Line215  # Draft 2D object (typed FeaturePython)
  ChamferSize = 0
  Closed = false
  End = (215.5,1,0)
  FilletRadius = 0
  Length = 47.25
  MakeFace = false
  Placement = pos=(168,1,0) rot=(0,0,1;0rad)
  Points = (2) [(0.25,-1.37668e-14,0),(47.5,-1.37668e-14,0)]
  Start = (168.25,1,0)
  Subdivisions = 0
FEATURE [Part::Part2DObjectPython] Line216  # Draft 2D object (typed FeaturePython)
  ChamferSize = 0
  Closed = false
  End = (250,1,0)
  FilletRadius = 0
  Length = 24.5
  MakeFace = false
  Placement = pos=(225,1,0) rot=(0,0,1;0rad)
  Points = (2) [(0.5,-1.77636e-14,0),(25,-1.77636e-14,0)]
  Start = (225.5,1,0)
  Subdivisions = 0
FEATURE [Part::Part2DObjectPython] Line217  # Draft 2D object (typed FeaturePython)
  ChamferSize = 0
  Closed = false
  End = (251,0,0)
  FilletRadius = 0
  Length = 78
  MakeFace = false
  Placement = pos=(251,-79,0) rot=(0,0,1;0rad)
  Points = (2) [(1.78814e-07,1,0),(0,79,0)]
  Start = (251,-78,0)
  Subdivisions = 0
FEATURE [Part::Part2DObjectPython] Line218  # Draft 2D object (typed FeaturePython)
  ChamferSize = 0
  Closed = false
  End = (-1,0,0)
  FilletRadius = 0
  Length = 78
  MakeFace = false
  Placement = pos=(-1,-79,0) rot=(0,0,1;0rad)
  Points = (2) [(7.10543e-15,1,0),(9.54792e-15,79,0)]
  Start = (-1,-78,0)
  Subdivisions = 0
FEATURE [Part::Part2DObjectPython] Line214  # Draft 2D object (typed FeaturePython)
  ChamferSize = 0
  Closed = false
  End = (158.25,1,0)
  FilletRadius = 0
  Length = 27.25
  MakeFace = false
  Placement = pos=(130,1,0) rot=(0,0,1;0rad)
  Points = (2) [(1,-2.93099e-14,0),(28.25,-2.93099e-14,0)]
  Start = (131,1,0)
  Subdivisions = 0
FEATURE [Part::Part2DObjectPython] Line219  # Draft 2D object (typed FeaturePython)
  ChamferSize = 0
  Closed = false
  End = (119,10,0)
  FilletRadius = 0
  Length = 9
  MakeFace = false
  Placement = pos=(119,1,0) rot=(0,0,1;0rad)
  Points = (2) [(0,0,0),(0,9,0)]
  Start = (119,1,0)
  Subdivisions = 0
FEATURE [Part::Part2DObjectPython] Line220  # Draft 2D object (typed FeaturePython)
  ChamferSize = 0
  Closed = false
  End = (131,10,0)
  FilletRadius = 0
  Length = 9
  MakeFace = false
  Placement = pos=(131,1,0) rot=(0,0,1;0rad)
  Points = (2) [(0,0,0),(0,9,0)]
  Start = (131,1,0)
  Subdivisions = 0
FEATURE [Part::Part2DObjectPython] Line221  # Draft 2D object (typed FeaturePython)
  ChamferSize = 0
  Closed = false
  End = (119,1,0)
  FilletRadius = 0
  Length = 27.25
  MakeFace = false
  Placement = pos=(91.5,1,0) rot=(0,0,1;0rad)
  Points = (2) [(0.25,-1.79856e-14,0),(27.5,-1.79856e-14,0)]
  Start = (91.75,1,0)
  Subdivisions = 0
FEATURE [Part::Part2DObjectPython] Line222  # Draft 2D object (typed FeaturePython)
  ChamferSize = 0
  Closed = false
  End = (77,-79,0)
  FilletRadius = 0
  Length = 47.25
  MakeFace = false
  Placement = pos=(29.5,-79,0) rot=(0,0,1;0rad)
  Points = (2) [(0.25,0,0),(47.5,0,0)]
  Start = (29.75,-79,0)
  Subdivisions = 0
FEATURE [Part::Part2DObjectPython] Line223  # Draft 2D object (typed FeaturePython)
  ChamferSize = 0
  Closed = false
  End = (164,-83,0)
  FilletRadius = 0
  Length = 3
  MakeFace = false
  Placement = pos=(164,-80,0) rot=(0,0,1;0rad)
  Points = (2) [(0,0,0),(0,-3,0)]
  Start = (164,-80,0)
  Subdivisions = 0
FEATURE [App::DocumentObjectGroup] Group006  label="Nub7"
  Group = -> [Arc031,Arc032,Arc033,Arc030,Line075,Line076,Line223]
FEATURE [Part::Part2DObjectPython] Line085  # Draft 2D object (typed FeaturePython)
  ChamferSize = 0
  Closed = false
  End = (0.5,-77,0)
  FilletRadius = 0
  Length = 76
  MakeFace = false
  Placement = pos=(0.5,-0.5,0) rot=(0,0,1;0rad)
  Points = (2) [(1.11022e-16,-0.5,0),(1.11022e-16,-76.5,0)]
  Start = (0.5,-1,0)
  Subdivisions = 0
FEATURE [Part::Part2DObjectPython] Line246  # Draft 2D object (typed FeaturePython)
  ChamferSize = 0
  Closed = false
  End = (43.5368,-59.0492,0)
  FilletRadius = 0
  Length = 18.05
  MakeFace = false
  Placement = pos=(25.4868,-59.0492,0) rot=(0,0,1;0rad)
  Points = (2) [(0,0,0),(18.05,7.10543e-15,0)]
  Start = (25.4868,-59.0492,0)
  Subdivisions = 0
FEATURE [Part::Part2DObjectPython] Line247  # Draft 2D object (typed FeaturePython)
  ChamferSize = 0
  Closed = false
  End = (224.512,-59.0492,0)
  FilletRadius = 0
  Length = 18.05
  MakeFace = false
  Placement = pos=(206.462,-59.0492,0) rot=(0,0,1;0rad)
  Points = (2) [(0,0,0),(18.05,0,0)]
  Start = (206.462,-59.0492,0)
  Subdivisions = 0
FEATURE [Part::Part2DObjectPython] Line248  # Draft 2D object (typed FeaturePython)
  ChamferSize = 0
  Closed = false
  End = (24.4868,-78,0)
  FilletRadius = 0
  Length = 22.9868
  MakeFace = false
  Placement = pos=(1.5,-78,0) rot=(0,0,1;0rad)
  Points = (2) [(0,0,0),(22.9868,0,0)]
  Start = (1.5,-78,0)
  Subdivisions = 0
FEATURE [Part::Part2DObjectPython] Line249  # Draft 2D object (typed FeaturePython)
  ChamferSize = 0
  Closed = false
  End = (205.462,-78,0)
  FilletRadius = 0
  Length = 160.925
  MakeFace = false
  Placement = pos=(44.5368,-78,0) rot=(0,0,1;0rad)
  Points = (2) [(0,0,0),(160.925,2.84217e-14,0)]
  Start = (44.5368,-78,0)
  Subdivisions = 0
FEATURE [Part::Part2DObjectPython] Line250  # Draft 2D object (typed FeaturePython)
  ChamferSize = 0
  Closed = false
  End = (248.5,-78,0)
  FilletRadius = 0
  Length = 22.988
  MakeFace = false
  Placement = pos=(225.512,-78,0) rot=(0,0,1;0rad)
  Points = (2) [(0,0,0),(22.988,-9.9476e-14,0)]
  Start = (225.512,-78,0)
  Subdivisions = 0
FEATURE [Part::Part2DObjectPython] Line251  # Draft 2D object (typed FeaturePython)
  ChamferSize = 0
  Closed = false
  End = (25.4868,-77,0)
  FilletRadius = 0
  Length = 17.9508
  MakeFace = false
  Placement = pos=(25.4868,-59.0492,0) rot=(0,0,1;0rad)
  Points = (2) [(0,0,0),(0,-17.9508,0)]
  Start = (25.4868,-59.0492,0)
  Subdivisions = 0
FEATURE [Part::Part2DObjectPython] Line252  # Draft 2D object (typed FeaturePython)
  ChamferSize = 0
  Closed = false
  End = (43.5368,-77,0)
  FilletRadius = 0
  Length = 17.9508
  MakeFace = false
  Placement = pos=(43.5368,-59.0492,0) rot=(0,0,1;0rad)
  Points = (2) [(0,0,0),(0,-17.9508,0)]
  Start = (43.5368,-59.0492,0)
  Subdivisions = 0
FEATURE [Part::Part2DObjectPython] Line253  # Draft 2D object (typed FeaturePython)
  ChamferSize = 0
  Closed = false
  End = (206.462,-77,0)
  FilletRadius = 0
  Length = 17.9508
  MakeFace = false
  Placement = pos=(206.462,-59.0492,0) rot=(0,0,1;0rad)
  Points = (2) [(0,0,0),(0,-17.9508,0)]
  Start = (206.462,-59.0492,0)
  Subdivisions = 0
FEATURE [Part::Part2DObjectPython] Line254  # Draft 2D object (typed FeaturePython)
  ChamferSize = 0
  Closed = false
  End = (224.512,-77,0)
  FilletRadius = 0
  Length = 17.9508
  MakeFace = false
  Placement = pos=(224.512,-59.0492,0) rot=(0,0,1;0rad)
  Points = (2) [(0,0,0),(0,-17.9508,0)]
  Start = (224.512,-59.0492,0)
  Subdivisions = 0
FEATURE [Part::Feature] Shape336
  Placement = pos=(-65.5951,-58.3077,0) rot=(0,0,1;0rad)
  shape: bbox 2e-07 x 4.701 x 2e-07 mm, 0 faces, 0 solids (baked)
FEATURE [Part::Feature] Shape337
  Placement = pos=(-65.5951,-58.3077,0) rot=(0,0,1;0rad)
  shape: bbox 1.525 x 2e-07 x 2e-07 mm, 0 faces, 0 solids (baked)
FEATURE [Part::Feature] Shape338
  Placement = pos=(-65.5951,-58.3077,0) rot=(0,0,1;0rad)
  shape: bbox 2e-07 x 3.23 x 2e-07 mm, 0 faces, 0 solids (baked)
FEATURE [Part::Feature] Shape339
  Placement = pos=(-65.5951,-58.3077,0) rot=(0,0,1;0rad)
  shape: bbox 1.726 x 2e-07 x 2e-07 mm, 0 faces, 0 solids (baked)
FEATURE [Part::Feature] Shape340
  Placement = pos=(-65.5951,-58.3077,0) rot=(0,0,1;0rad)
  shape: bbox 2e-07 x 0.9219 x 2e-07 mm, 0 faces, 0 solids (baked)
FEATURE [Part::Feature] Shape341
  Placement = pos=(-65.5951,-58.3077,0) rot=(0,0,1;0rad)
  shape: bbox 3.299 x 2e-07 x 2e-07 mm, 0 faces, 0 solids (baked)
FEATURE [Part::Feature] Shape342
  Placement = pos=(-65.5951,-58.3077,0) rot=(0,0,1;0rad)
  shape: bbox 2e-07 x 0.9219 x 2e-07 mm, 0 faces, 0 solids (baked)
FEATURE [Part::Feature] Shape343
  Placement = pos=(-65.5951,-58.3077,0) rot=(0,0,1;0rad)
  shape: bbox 1.725 x 2e-07 x 2e-07 mm, 0 faces, 0 solids (baked)
FEATURE [Part::Feature] Shape344
  Placement = pos=(-65.5951,-58.3077,0) rot=(0,0,1;0rad)
  shape: bbox 2e-07 x 3.23 x 2e-07 mm, 0 faces, 0 solids (baked)
FEATURE [Part::Feature] Shape345
  Placement = pos=(-65.5951,-58.3077,0) rot=(0,0,1;0rad)
  shape: bbox 0.8255 x 2e-07 x 2e-07 mm, 0 faces, 0 solids (baked)
FEATURE [Part::Feature] Shape346
  Placement = pos=(-65.5951,-58.3077,0) rot=(0,0,1;0rad)
  shape: bbox 2e-07 x 2.799 x 2e-07 mm, 0 faces, 0 solids (baked)
FEATURE [Part::Feature] Shape347
  Placement = pos=(-65.5951,-58.3077,0) rot=(0,0,1;0rad)
  shape: bbox 0.8255 x 2e-07 x 2e-07 mm, 0 faces, 0 solids (baked)
FEATURE [Part::Feature] Shape348
  Placement = pos=(-65.5951,-58.3077,0) rot=(0,0,1;0rad)
  shape: bbox 2e-07 x 6.27 x 2e-07 mm, 0 faces, 0 solids (baked)
FEATURE [Part::Feature] Shape349
  Placement = pos=(-65.5951,-58.3077,0) rot=(0,0,1;0rad)
  shape: bbox 1.725 x 2e-07 x 2e-07 mm, 0 faces, 0 solids (baked)
FEATURE [Part::Feature] Shape350
  Placement = pos=(-65.5951,-58.3077,0) rot=(0,0,1;0rad)
  shape: bbox 2e-07 x 0.9812 x 2e-07 mm, 0 faces, 0 solids (baked)
FEATURE [Part::Feature] Shape351
  Placement = pos=(-65.5951,-58.3077,0) rot=(0,0,1;0rad)
  shape: bbox 3.299 x 2e-07 x 2e-07 mm, 0 faces, 0 solids (baked)
FEATURE [Part::Feature] Shape352
  Placement = pos=(-65.5951,-58.3077,0) rot=(0,0,1;0rad)
  shape: bbox 2e-07 x 0.9812 x 2e-07 mm, 0 faces, 0 solids (baked)
FEATURE [Part::Feature] Shape353
  Placement = pos=(-65.5951,-58.3077,0) rot=(0,0,1;0rad)
  shape: bbox 1.726 x 2e-07 x 2e-07 mm, 0 faces, 0 solids (baked)
FEATURE [Part::Feature] Shape354
  Placement = pos=(-65.5951,-58.3077,0) rot=(0,0,1;0rad)
  shape: bbox 2e-07 x 4.469 x 2e-07 mm, 0 faces, 0 solids (baked)
FEATURE [Part::Feature] Shape355
  Placement = pos=(-65.5951,-58.3077,0) rot=(0,0,1;0rad)
  shape: bbox 1.525 x 2e-07 x 2e-07 mm, 0 faces, 0 solids (baked)
FEATURE [Part::Feature] Shape356
  Placement = pos=(-65.5951,-58.3077,0) rot=(0,0,1;0rad)
  shape: bbox 2e-07 x 4.699 x 2e-07 mm, 0 faces, 0 solids (baked)
FEATURE [Part::Feature] Shape357
  Placement = pos=(-65.5951,-58.3077,0) rot=(0,0,1;0rad)
  shape: bbox 14 x 2e-07 x 2e-07 mm, 0 faces, 0 solids (baked)
FEATURE [Part::Feature] Shape358
  Placement = pos=(-65.5951,-58.3077,0) rot=(0,0,1;0rad)
  shape: bbox 2e-07 x 4.699 x 2e-07 mm, 0 faces, 0 solids (baked)
FEATURE [Part::Feature] Shape359
  Placement = pos=(-65.5951,-58.3077,0) rot=(0,0,1;0rad)
  shape: bbox 1.526 x 2e-07 x 2e-07 mm, 0 faces, 0 solids (baked)
FEATURE [Part::Feature] Shape360
  Placement = pos=(-65.5951,-58.3077,0) rot=(0,0,1;0rad)
  shape: bbox 2e-07 x 4.469 x 2e-07 mm, 0 faces, 0 solids (baked)
FEATURE [Part::Feature] Shape361
  Placement = pos=(-65.5951,-58.3077,0) rot=(0,0,1;0rad)
  shape: bbox 1.724 x 2e-07 x 2e-07 mm, 0 faces, 0 solids (baked)
FEATURE [Part::Feature] Shape362
  Placement = pos=(-65.5951,-58.3077,0) rot=(0,0,1;0rad)
  shape: bbox 2e-07 x 0.9812 x 2e-07 mm, 0 faces, 0 solids (baked)
FEATURE [Part::Feature] Shape363
  Placement = pos=(-65.5951,-58.3077,0) rot=(0,0,1;0rad)
  shape: bbox 3.3 x 2e-07 x 2e-07 mm, 0 faces, 0 solids (baked)
FEATURE [Part::Feature] Shape364
  Placement = pos=(-65.5951,-58.3077,0) rot=(0,0,1;0rad)
  shape: bbox 2e-07 x 0.9812 x 2e-07 mm, 0 faces, 0 solids (baked)
FEATURE [Part::Feature] Shape365
  Placement = pos=(-65.5951,-58.3077,0) rot=(0,0,1;0rad)
  shape: bbox 1.725 x 2e-07 x 2e-07 mm, 0 faces, 0 solids (baked)
FEATURE [Part::Feature] Shape366
  Placement = pos=(-65.5951,-58.3077,0) rot=(0,0,1;0rad)
  shape: bbox 2e-07 x 6.27 x 2e-07 mm, 0 faces, 0 solids (baked)
FEATURE [Part::Feature] Shape367
  Placement = pos=(-65.5951,-58.3077,0) rot=(0,0,1;0rad)
  shape: bbox 0.826 x 2e-07 x 2e-07 mm, 0 faces, 0 solids (baked)
FEATURE [Part::Feature] Shape368
  Placement = pos=(-65.5951,-58.3077,0) rot=(0,0,1;0rad)
  shape: bbox 2e-07 x 2.799 x 2e-07 mm, 0 faces, 0 solids (baked)
FEATURE [Part::Feature] Shape369
  Placement = pos=(-65.5951,-58.3077,0) rot=(0,0,1;0rad)
  shape: bbox 0.826 x 2e-07 x 2e-07 mm, 0 faces, 0 solids (baked)
FEATURE [Part::Feature] Shape370
  Placement = pos=(-65.5951,-58.3077,0) rot=(0,0,1;0rad)
  shape: bbox 2e-07 x 3.23 x 2e-07 mm, 0 faces, 0 solids (baked)
FEATURE [Part::Feature] Shape371
  Placement = pos=(-65.5951,-58.3077,0) rot=(0,0,1;0rad)
  shape: bbox 1.725 x 2e-07 x 2e-07 mm, 0 faces, 0 solids (baked)
FEATURE [Part::Feature] Shape372
  Placement = pos=(-65.5951,-58.3077,0) rot=(0,0,1;0rad)
  shape: bbox 2e-07 x 0.9219 x 2e-07 mm, 0 faces, 0 solids (baked)
FEATURE [Part::Feature] Shape373
  Placement = pos=(-65.5951,-58.3077,0) rot=(0,0,1;0rad)
  shape: bbox 3.3 x 2e-07 x 2e-07 mm, 0 faces, 0 solids (baked)
FEATURE [Part::Feature] Shape374
  Placement = pos=(-65.5951,-58.3077,0) rot=(0,0,1;0rad)
  shape: bbox 2e-07 x 0.9219 x 2e-07 mm, 0 faces, 0 solids (baked)
FEATURE [Part::Feature] Shape375
  Placement = pos=(-65.5951,-58.3077,0) rot=(0,0,1;0rad)
  shape: bbox 1.724 x 2e-07 x 2e-07 mm, 0 faces, 0 solids (baked)
FEATURE [Part::Feature] Shape376
  Placement = pos=(-65.5951,-58.3077,0) rot=(0,0,1;0rad)
  shape: bbox 2e-07 x 3.23 x 2e-07 mm, 0 faces, 0 solids (baked)
FEATURE [Part::Feature] Shape377
  Placement = pos=(-65.5951,-58.3077,0) rot=(0,0,1;0rad)
  shape: bbox 1.526 x 2e-07 x 2e-07 mm, 0 faces, 0 solids (baked)
FEATURE [Part::Feature] Shape378
  Placement = pos=(-65.5951,-58.3077,0) rot=(0,0,1;0rad)
  shape: bbox 2e-07 x 4.701 x 2e-07 mm, 0 faces, 0 solids (baked)
FEATURE [Part::Feature] Shape379
  Placement = pos=(-65.5951,-58.3077,0) rot=(0,0,1;0rad)
  shape: bbox 14 x 2e-07 x 2e-07 mm, 0 faces, 0 solids (baked)
FEATURE [Part::Part2DObjectPython] Line255  # Draft 2D object (typed FeaturePython)
  ChamferSize = 0
  Closed = false
  End = (22.4617,-10.4241,0)
  FilletRadius = 0
  Length = 13.9995
  MakeFace = false
  Placement = pos=(8.46212,-10.4241,0) rot=(0,0,1;0rad)
  Points = (2) [(0,0,0),(13.9995,1.77636e-15,0)]
  Start = (8.46212,-10.4241,0)
  Subdivisions = 0
FEATURE [Part::Part2DObjectPython] Line256  # Draft 2D object (typed FeaturePython)
  ChamferSize = 0
  Closed = false
  End = (15.4619,-3.4245,0)
  FilletRadius = 0
  Length = 13.9993
  MakeFace = false
  Placement = pos=(15.4619,-17.4238,0) rot=(0,0,1;0rad)
  Points = (2) [(0,0,0),(1.77636e-15,13.9993,0)]
  Start = (15.4619,-17.4238,0)
  Subdivisions = 0
FEATURE [Part::Part2DObjectPython] Line257  # Draft 2D object (typed FeaturePython)
  ChamferSize = 0
  Closed = false
  End = (13.0806,-60.5745,0)
  FilletRadius = 0
  Length = 13.9995
  MakeFace = false
  Placement = pos=(13.0806,-74.574,0) rot=(0,0,1;0rad)
  Points = (2) [(0,0,0),(0,13.9995,0)]
  Start = (13.0806,-74.574,0)
  Subdivisions = 0
FEATURE [Part::Part2DObjectPython] Line258  # Draft 2D object (typed FeaturePython)
  ChamferSize = 0
  Closed = false
  End = (20.0804,-67.5742,0)
  FilletRadius = 0
  Length = 13.9995
  MakeFace = false
  Placement = pos=(6.08087,-67.5742,0) rot=(0,0,1;0rad)
  Points = (2) [(0,0,0),(13.9995,0,0)]
  Start = (6.08087,-67.5742,0)
  Subdivisions = 0
FEATURE [Part::Part2DObjectPython] Line259  # Draft 2D object (typed FeaturePython)
  ChamferSize = 0
  Closed = false
  End = (243.918,-67.5742,0)
  FilletRadius = 0
  Length = 14.001
  MakeFace = false
  Placement = pos=(229.917,-67.5742,0) rot=(0,0,1;0rad)
  Points = (2) [(0,0,0),(14.001,-5.68434e-14,0)]
  Start = (229.917,-67.5742,0)
  Subdivisions = 0
FEATURE [Part::Part2DObjectPython] Line260  # Draft 2D object (typed FeaturePython)
  ChamferSize = 0
  Closed = false
  End = (236.917,-60.5745,0)
  FilletRadius = 0
  Length = 13.9995
  MakeFace = false
  Placement = pos=(236.917,-74.574,0) rot=(0,0,1;0rad)
  Points = (2) [(0,0,0),(0,13.9995,0)]
  Start = (236.917,-74.574,0)
  Subdivisions = 0
FEATURE [Part::Part2DObjectPython] Line261  # Draft 2D object (typed FeaturePython)
  ChamferSize = 0
  Closed = false
  End = (234.537,-3.4245,0)
  FilletRadius = 0
  Length = 13.9993
  MakeFace = false
  Placement = pos=(234.537,-17.4238,0) rot=(0,0,1;0rad)
  Points = (2) [(0,0,0),(0,13.9993,0)]
  Start = (234.537,-17.4238,0)
  Subdivisions = 0
FEATURE [Part::Part2DObjectPython] Line262  # Draft 2D object (typed FeaturePython)
  ChamferSize = 0
  Closed = false
  End = (241.537,-10.4241,0)
  FilletRadius = 0
  Length = 14
  MakeFace = false
  Placement = pos=(227.537,-10.4241,0) rot=(0,0,1;0rad)
  Points = (2) [(0,0,0),(14,0,0)]
  Start = (227.537,-10.4241,0)
  Subdivisions = 0
FEATURE [Part::Part2DObjectPython] Line263  # Draft 2D object (typed FeaturePython)
  ChamferSize = 0
  Closed = false
  End = (122.474,-10.4241,0)
  FilletRadius = 0
  Length = 13.999
  MakeFace = false
  Placement = pos=(108.475,-10.4241,0) rot=(0,0,1;0rad)
  Points = (2) [(0,0,0),(13.999,0,0)]
  Start = (108.475,-10.4241,0)
  Subdivisions = 0
FEATURE [Part::Part2DObjectPython] Line264  # Draft 2D object (typed FeaturePython)
  ChamferSize = 0
  Closed = false
  End = (115.474,-3.4245,0)
  FilletRadius = 0
  Length = 13.9993
  MakeFace = false
  Placement = pos=(115.474,-17.4238,0) rot=(0,0,1;0rad)
  Points = (2) [(0,0,0),(0,13.9993,0)]
  Start = (115.474,-17.4238,0)
  Subdivisions = 0
FEATURE [Part::Part2DObjectPython] Line265  # Draft 2D object (typed FeaturePython)
  ChamferSize = 0
  Closed = false
  End = (141.524,-10.4241,0)
  FilletRadius = 0
  Length = 13.999
  MakeFace = false
  Placement = pos=(127.525,-10.4241,0) rot=(0,0,1;0rad)
  Points = (2) [(0,0,0),(13.999,1.77636e-15,0)]
  Start = (127.525,-10.4241,0)
  Subdivisions = 0
FEATURE [Part::Part2DObjectPython] Line266  # Draft 2D object (typed FeaturePython)
  ChamferSize = 0
  Closed = false
  End = (134.524,-3.4245,0)
  FilletRadius = 0
  Length = 13.9993
  MakeFace = false
  Placement = pos=(134.524,-17.4238,0) rot=(0,0,1;0rad)
  Points = (2) [(0,0,0),(0,13.9993,0)]
  Start = (134.524,-17.4238,0)
  Subdivisions = 0
FEATURE [App::DocumentObjectGroup] Group026  label="Plate"
  Group = -> [Shape004,Shape005,Shape006,Shape007,Shape008,Shape009,Shape010,Shape011,Shape012,Shape013,Shape014,Shape015,Shape016,Shape017,Shape018,Shape019,Shape020,Shape021,Shape022,Shape023,Shape024,Shape025,Shape026,Shape027,Shape028,Shape029,Shape030,Shape031,Shape032,Shape033,Shape034,Shape035,Shape036,Shape037,Shape038,Shape039,Shape040,Shape041,Shape042,Shape043,Shape044,Shape045,Shape046,Shape047,+300 more]
FEATURE [Part::Part2DObjectPython] Line269  # Draft 2D object (typed FeaturePython)
  ChamferSize = 0
  Closed = false
  End = (255,10,0)
  FilletRadius = 0
  Length = 124
  MakeFace = false
  Placement = pos=(131,10,0) rot=(0,0,1;0rad)
  Points = (2) [(0,0,0),(124,-8.88178e-15,0)]
  Start = (131,10,0)
  Subdivisions = 0
FEATURE [Part::Part2DObjectPython] Line271  # Draft 2D object (typed FeaturePython)
  ChamferSize = 0
  Closed = false
  End = (257,-86,0)
  FilletRadius = 0
  Length = 94
  MakeFace = false
  Placement = pos=(257,10,0) rot=(0,0,1;0rad)
  Points = (2) [(1.78814e-07,-2,0),(1.78814e-07,-96,0)]
  Start = (257,8,0)
  Subdivisions = 0
FEATURE [Part::Part2DObjectPython] Line273  # Draft 2D object (typed FeaturePython)
  ChamferSize = 0
  Closed = false
  End = (-5,-88,0)
  FilletRadius = 0
  Length = 260
  MakeFace = false
  Placement = pos=(255,-88,0) rot=(0,0,1;0rad)
  Points = (2) [(1.78814e-07,1.42109e-14,0),(-260,1.42109e-14,0)]
  Start = (255,-88,0)
  Subdivisions = 0
FEATURE [Part::Part2DObjectPython] Line274  # Draft 2D object (typed FeaturePython)
  ChamferSize = 0
  Closed = false
  End = (-5,10,0)
  FilletRadius = 0
  Length = 124
  MakeFace = false
  Placement = pos=(119,10,0) rot=(0,0,1;0rad)
  Points = (2) [(0,-7.10543e-15,0),(-124,-7.10543e-15,0)]
  Start = (119,10,0)
  Subdivisions = 0
FEATURE [Part::Part2DObjectPython] Line275  # Draft 2D object (typed FeaturePython)
  ChamferSize = 0
  Closed = false
  End = (-7,8,0)
  FilletRadius = 0
  Length = 94
  MakeFace = false
  Placement = pos=(-7,-88,0) rot=(0,0,1;0rad)
  Points = (2) [(5.32907e-15,2,0),(5.32907e-15,96,0)]
  Start = (-7,-86,0)
  Subdivisions = 0
FEATURE [Part::Part2DObjectPython] Arc048  # Draft 2D object (typed FeaturePython)
  FirstAngle = 90
  LastAngle = 180
  MakeFace = false
  Placement = pos=(-5,8,0) rot=(0,0,1;0rad)
  Radius = 2
FEATURE [Part::Part2DObjectPython] Arc049  # Draft 2D object (typed FeaturePython)
  FirstAngle = -180
  LastAngle = -90
  MakeFace = false
  Placement = pos=(-5,-86,0) rot=(0,0,1;0rad)
  Radius = 2
FEATURE [Part::Part2DObjectPython] Arc050  # Draft 2D object (typed FeaturePython)
  FirstAngle = -90
  LastAngle = 0
  MakeFace = false
  Placement = pos=(255,-86,0) rot=(0,0,1;0rad)
  Radius = 2
FEATURE [Part::Part2DObjectPython] Arc051  # Draft 2D object (typed FeaturePython)
  FirstAngle = 0
  LastAngle = 90
  MakeFace = false
  Placement = pos=(255,8,0) rot=(0,0,1;0rad)
  Radius = 2
FEATURE [Part::Part2DObjectPython] Circle  # Draft 2D object (typed FeaturePython)
  FirstAngle = 0
  LastAngle = 0
  MakeFace = false
  Placement = pos=(105.375,5.5,0) rot=(0,0,1;0rad)
  Radius = 1.85
FEATURE [Part::Part2DObjectPython] Circle001  # Draft 2D object (typed FeaturePython)
  FirstAngle = 0
  LastAngle = 0
  MakeFace = false
  Placement = pos=(144.625,5.5,0) rot=(0,0,1;0rad)
  Radius = 1.85
FEATURE [Part::Part2DObjectPython] Circle002  # Draft 2D object (typed FeaturePython)
  FirstAngle = 0
  LastAngle = 0
  MakeFace = false
  Placement = pos=(125,-83.5,0) rot=(0,0,1;0rad)
  Radius = 1.85
FEATURE [Part::Part2DObjectPython] Circle005  # Draft 2D object (typed FeaturePython)
  FirstAngle = 0
  LastAngle = 0
  MakeFace = false
  Placement = pos=(-2.5,5.5,0) rot=(0,0,1;0rad)
  Radius = 1.85
FEATURE [Part::Part2DObjectPython] Circle006  # Draft 2D object (typed FeaturePython)
  FirstAngle = 0
  LastAngle = 0
  MakeFace = false
  Placement = pos=(-2.5,-83.5,0) rot=(0,0,1;0rad)
  Radius = 1.85
FEATURE [Part::Part2DObjectPython] Circle007  # Draft 2D object (typed FeaturePython)
  FirstAngle = 0
  LastAngle = 0
  MakeFace = false
  Placement = pos=(252.5,5.5,0) rot=(0,0,1;0rad)
  Radius = 1.85
FEATURE [Part::Part2DObjectPython] Circle008  # Draft 2D object (typed FeaturePython)
  FirstAngle = 0
  LastAngle = 0
  MakeFace = false
  Placement = pos=(252.5,-83.5,0) rot=(0,0,1;0rad)
  Radius = 1.85
FEATURE [App::DocumentObjectGroup] Group028  label="Outside"
  Group = -> [Line269,Line271,Line273,Line274,Line275,Arc048,Arc049,Arc050,Arc051,Circle,Circle001,Circle002,Circle005,Circle006,Circle007,Circle008]
FEATURE [App::DocumentObjectGroup] Group012  label="Gasket"
  Group = -> [Group009,Group008,Line082,Group007,Line078,Group006,Group005,Group004,Group003,Group002,Group001,Group,Line038,Line030,Line,Line212,Line214,Line215,Line216,Line217,Line218,Line219,Line220,Line221,Line222,Group028]
FEATURE [Part::Part2DObjectPython] Circle009  # Draft 2D object (typed FeaturePython)
  FirstAngle = 0
  LastAngle = 0
  MakeFace = false
  Placement = pos=(252.5,5.5,0) rot=(0,0,1;0rad)
  Radius = 1.85
FEATURE [Part::Part2DObjectPython] Line276  # Draft 2D object (typed FeaturePython)
  ChamferSize = 0
  Closed = false
  End = (257,-86,0)
  FilletRadius = 0
  Length = 94
  MakeFace = false
  Placement = pos=(257,10,0) rot=(0,0,1;0rad)
  Points = (2) [(1.78814e-07,-2,0),(1.78814e-07,-96,0)]
  Start = (257,8,0)
  Subdivisions = 0
FEATURE [Part::Part2DObjectPython] Circle010  # Draft 2D object (typed FeaturePython)
  FirstAngle = 0
  LastAngle = 0
  MakeFace = false
  Placement = pos=(125,-83.5,0) rot=(0,0,1;0rad)
  Radius = 1.85
FEATURE [Part::Part2DObjectPython] Arc052  # Draft 2D object (typed FeaturePython)
  FirstAngle = -180
  LastAngle = -90
  MakeFace = false
  Placement = pos=(-5,-86,0) rot=(0,0,1;0rad)
  Radius = 2
FEATURE [Part::Part2DObjectPython] Line278  # Draft 2D object (typed FeaturePython)
  ChamferSize = 0
  Closed = false
  End = (-5,-88,0)
  FilletRadius = 0
  Length = 260
  MakeFace = false
  Placement = pos=(255,-88,0) rot=(0,0,1;0rad)
  Points = (2) [(1.78814e-07,1.42109e-14,0),(-260,1.42109e-14,0)]
  Start = (255,-88,0)
  Subdivisions = 0
FEATURE [Part::Part2DObjectPython] Line280  # Draft 2D object (typed FeaturePython)
  ChamferSize = 0
  Closed = false
  End = (-7,8,0)
  FilletRadius = 0
  Length = 94
  MakeFace = false
  Placement = pos=(-7,-88,0) rot=(0,0,1;0rad)
  Points = (2) [(5.32907e-15,2,0),(5.32907e-15,96,0)]
  Start = (-7,-86,0)
  Subdivisions = 0
FEATURE [Part::Part2DObjectPython] Arc053  # Draft 2D object (typed FeaturePython)
  FirstAngle = 90
  LastAngle = 180
  MakeFace = false
  Placement = pos=(-5,8,0) rot=(0,0,1;0rad)
  Radius = 2
FEATURE [Part::Part2DObjectPython] Arc054  # Draft 2D object (typed FeaturePython)
  FirstAngle = -90
  LastAngle = 0
  MakeFace = false
  Placement = pos=(255,-86,0) rot=(0,0,1;0rad)
  Radius = 2
FEATURE [Part::Part2DObjectPython] Arc055  # Draft 2D object (typed FeaturePython)
  FirstAngle = 0
  LastAngle = 90
  MakeFace = false
  Placement = pos=(255,8,0) rot=(0,0,1;0rad)
  Radius = 2
FEATURE [Part::Part2DObjectPython] Circle012  # Draft 2D object (typed FeaturePython)
  FirstAngle = 0
  LastAngle = 0
  MakeFace = false
  Placement = pos=(105.375,5.5,0) rot=(0,0,1;0rad)
  Radius = 1.85
FEATURE [Part::Part2DObjectPython] Circle013  # Draft 2D object (typed FeaturePython)
  FirstAngle = 0
  LastAngle = 0
  MakeFace = false
  Placement = pos=(144.625,5.5,0) rot=(0,0,1;0rad)
  Radius = 1.85
FEATURE [Part::Part2DObjectPython] Circle014  # Draft 2D object (typed FeaturePython)
  FirstAngle = 0
  LastAngle = 0
  MakeFace = false
  Placement = pos=(-2.5,5.5,0) rot=(0,0,1;0rad)
  Radius = 1.85
FEATURE [Part::Part2DObjectPython] Circle015  # Draft 2D object (typed FeaturePython)
  FirstAngle = 0
  LastAngle = 0
  MakeFace = false
  Placement = pos=(-2.5,-83.5,0) rot=(0,0,1;0rad)
  Radius = 1.85
FEATURE [Part::Part2DObjectPython] Circle016  # Draft 2D object (typed FeaturePython)
  FirstAngle = 0
  LastAngle = 0
  MakeFace = false
  Placement = pos=(252.5,-83.5,0) rot=(0,0,1;0rad)
  Radius = 1.85
FEATURE [Part::Part2DObjectPython] Line281  # Draft 2D object (typed FeaturePython)
  ChamferSize = 0
  Closed = false
  End = (255,10,0)
  FilletRadius = 0
  Length = 260
  MakeFace = false
  Placement = pos=(-5,10,0) rot=(0,0,1;0rad)
  Points = (2) [(0,0,0),(260,8.88178e-15,0)]
  Start = (-5,10,0)
  Subdivisions = 0
FEATURE [App::DocumentObjectGroup] Group029  label="Outside001"
  Group = -> [Line276,Line278,Line280,Arc053,Arc052,Arc054,Arc055,Circle012,Circle013,Circle010,Circle014,Circle015,Circle009,Circle016,Line281]
FEATURE [App::DocumentObjectGroup] Group010  label="Mid"
  Group = -> [Line084,Line085,Line087,Arc040,Arc041,Arc042,Arc043,Arc044,Arc045,Arc046,Arc047,Line246,Line247,Line248,Line249,Line250,Line251,Line252,Line253,Line254,Group029]
FEATURE [Part::Part2DObjectPython] Line282  # Draft 2D object (typed FeaturePython)
  ChamferSize = 0
  Closed = false
  End = (0.5,-77,0)
  FilletRadius = 0
  Length = 76
  MakeFace = false
  Placement = pos=(0.5,-0.5,0) rot=(0,0,1;0rad)
  Points = (2) [(1.11022e-16,-0.5,0),(1.11022e-16,-76.5,0)]
  Start = (0.5,-1,0)
  Subdivisions = 0
FEATURE [Part::Part2DObjectPython] Line283  # Draft 2D object (typed FeaturePython)
  ChamferSize = 0
  Closed = false
  End = (43.5368,-59.0492,0)
  FilletRadius = 0
  Length = 18.05
  MakeFace = false
  Placement = pos=(25.4868,-59.0492,0) rot=(0,0,1;0rad)
  Points = (2) [(0,0,0),(18.05,7.10543e-15,0)]
  Start = (25.4868,-59.0492,0)
  Subdivisions = 0
FEATURE [Part::Part2DObjectPython] Line284  # Draft 2D object (typed FeaturePython)
  ChamferSize = 0
  Closed = false
  End = (224.512,-59.0492,0)
  FilletRadius = 0
  Length = 18.05
  MakeFace = false
  Placement = pos=(206.462,-59.0492,0) rot=(0,0,1;0rad)
  Points = (2) [(0,0,0),(18.05,0,0)]
  Start = (206.462,-59.0492,0)
  Subdivisions = 0
FEATURE [Part::Part2DObjectPython] Line285  # Draft 2D object (typed FeaturePython)
  ChamferSize = 0
  Closed = false
  End = (24.4868,-78,0)
  FilletRadius = 0
  Length = 22.9868
  MakeFace = false
  Placement = pos=(1.5,-78,0) rot=(0,0,1;0rad)
  Points = (2) [(0,0,0),(22.9868,0,0)]
  Start = (1.5,-78,0)
  Subdivisions = 0
FEATURE [Part::Part2DObjectPython] Line286  # Draft 2D object (typed FeaturePython)
  ChamferSize = 0
  Closed = false
  End = (205.462,-78,0)
  FilletRadius = 0
  Length = 160.925
  MakeFace = false
  Placement = pos=(44.5368,-78,0) rot=(0,0,1;0rad)
  Points = (2) [(0,0,0),(160.925,2.84217e-14,0)]
  Start = (44.5368,-78,0)
  Subdivisions = 0
FEATURE [Part::Part2DObjectPython] Line287  # Draft 2D object (typed FeaturePython)
  ChamferSize = 0
  Closed = false
  End = (248.5,-78,0)
  FilletRadius = 0
  Length = 22.988
  MakeFace = false
  Placement = pos=(225.512,-78,0) rot=(0,0,1;0rad)
  Points = (2) [(0,0,0),(22.988,-9.9476e-14,0)]
  Start = (225.512,-78,0)
  Subdivisions = 0
FEATURE [Part::Part2DObjectPython] Line288  # Draft 2D object (typed FeaturePython)
  ChamferSize = 0
  Closed = false
  End = (25.4868,-77,0)
  FilletRadius = 0
  Length = 17.9508
  MakeFace = false
  Placement = pos=(25.4868,-59.0492,0) rot=(0,0,1;0rad)
  Points = (2) [(0,0,0),(0,-17.9508,0)]
  Start = (25.4868,-59.0492,0)
  Subdivisions = 0
FEATURE [Part::Part2DObjectPython] Line289  # Draft 2D object (typed FeaturePython)
  ChamferSize = 0
  Closed = false
  End = (43.5368,-77,0)
  FilletRadius = 0
  Length = 17.9508
  MakeFace = false
  Placement = pos=(43.5368,-59.0492,0) rot=(0,0,1;0rad)
  Points = (2) [(0,0,0),(0,-17.9508,0)]
  Start = (43.5368,-59.0492,0)
  Subdivisions = 0
FEATURE [Part::Part2DObjectPython] Line290  # Draft 2D object (typed FeaturePython)
  ChamferSize = 0
  Closed = false
  End = (206.462,-77,0)
  FilletRadius = 0
  Length = 17.9508
  MakeFace = false
  Placement = pos=(206.462,-59.0492,0) rot=(0,0,1;0rad)
  Points = (2) [(0,0,0),(0,-17.9508,0)]
  Start = (206.462,-59.0492,0)
  Subdivisions = 0
FEATURE [Part::Part2DObjectPython] Line291  # Draft 2D object (typed FeaturePython)
  ChamferSize = 0
  Closed = false
  End = (224.512,-77,0)
  FilletRadius = 0
  Length = 17.9508
  MakeFace = false
  Placement = pos=(224.512,-59.0492,0) rot=(0,0,1;0rad)
  Points = (2) [(0,0,0),(0,-17.9508,0)]
  Start = (224.512,-59.0492,0)
  Subdivisions = 0
FEATURE [Part::Part2DObjectPython] Circle017  # Draft 2D object (typed FeaturePython)
  FirstAngle = 0
  LastAngle = 0
  MakeFace = false
  Placement = pos=(-2.5,-83.5,0) rot=(0,0,1;0rad)
  Radius = 1.25
FEATURE [Part::Part2DObjectPython] Circle018  # Draft 2D object (typed FeaturePython)
  FirstAngle = 0
  LastAngle = 0
  MakeFace = false
  Placement = pos=(252.5,-83.5,0) rot=(0,0,1;0rad)
  Radius = 1.25
FEATURE [Part::Part2DObjectPython] Arc056  # Draft 2D object (typed FeaturePython)
  FirstAngle = -180
  LastAngle = -90
  MakeFace = false
  Placement = pos=(-5,-86,0) rot=(0,0,1;0rad)
  Radius = 2
FEATURE [Part::Part2DObjectPython] Arc057  # Draft 2D object (typed FeaturePython)
  FirstAngle = -180
  LastAngle = -90
  MakeFace = false
  Placement = pos=(44.5368,-77,0) rot=(0,0,1;0rad)
  Radius = 1
FEATURE [Part::Part2DObjectPython] Line292  # Draft 2D object (typed FeaturePython)
  ChamferSize = 0
  Closed = false
  End = (-5,-88,0)
  FilletRadius = 0
  Length = 260
  MakeFace = false
  Placement = pos=(255,-88,0) rot=(0,0,1;0rad)
  Points = (2) [(1.78814e-07,1.42109e-14,0),(-260,1.42109e-14,0)]
  Start = (255,-88,0)
  Subdivisions = 0
FEATURE [Part::Part2DObjectPython] Arc058  # Draft 2D object (typed FeaturePython)
  FirstAngle = 0
  LastAngle = 90
  MakeFace = false
  Placement = pos=(255,8,0) rot=(0,0,1;0rad)
  Radius = 2
FEATURE [Part::Part2DObjectPython] Line293  # Draft 2D object (typed FeaturePython)
  ChamferSize = 0
  Closed = false
  End = (257,-86,0)
  FilletRadius = 0
  Length = 94
  MakeFace = false
  Placement = pos=(257,10,0) rot=(0,0,1;0rad)
  Points = (2) [(1.78814e-07,-2,0),(1.78814e-07,-96,0)]
  Start = (257,8,0)
  Subdivisions = 0
FEATURE [Part::Part2DObjectPython] Arc059  # Draft 2D object (typed FeaturePython)
  FirstAngle = -180
  LastAngle = -90
  MakeFace = false
  Placement = pos=(225.512,-77,0) rot=(0,0,1;0rad)
  Radius = 1
FEATURE [Part::Part2DObjectPython] Arc060  # Draft 2D object (typed FeaturePython)
  FirstAngle = 90
  LastAngle = 180
  MakeFace = false
  Placement = pos=(24.4868,-77,0) rot=(0,0,1;3.14159rad)
  Radius = 1
FEATURE [Part::Part2DObjectPython] Arc061  # Draft 2D object (typed FeaturePython)
  FirstAngle = 90
  LastAngle = 180
  MakeFace = false
  Placement = pos=(205.462,-77,0) rot=(0,0,1;3.14159rad)
  Radius = 1
FEATURE [Part::Part2DObjectPython] Line294  # Draft 2D object (typed FeaturePython)
  ChamferSize = 0
  Closed = false
  End = (-7,8,0)
  FilletRadius = 0
  Length = 94
  MakeFace = false
  Placement = pos=(-7,-88,0) rot=(0,0,1;0rad)
  Points = (2) [(5.32907e-15,2,0),(5.32907e-15,96,0)]
  Start = (-7,-86,0)
  Subdivisions = 0
FEATURE [Part::Part2DObjectPython] Circle020  # Draft 2D object (typed FeaturePython)
  FirstAngle = 0
  LastAngle = 0
  MakeFace = false
  Placement = pos=(252.5,5.5,0) rot=(0,0,1;0rad)
  Radius = 1.25
FEATURE [Part::Part2DObjectPython] Arc062  # Draft 2D object (typed FeaturePython)
  FirstAngle = -90
  LastAngle = 0
  MakeFace = false
  Placement = pos=(255,-86,0) rot=(0,0,1;0rad)
  Radius = 2
FEATURE [Part::Part2DObjectPython] Arc063  # Draft 2D object (typed FeaturePython)
  FirstAngle = 90
  LastAngle = 180
  MakeFace = false
  Placement = pos=(-5,8,0) rot=(0,0,1;0rad)
  Radius = 2
FEATURE [Part::Part2DObjectPython] Circle021  # Draft 2D object (typed FeaturePython)
  FirstAngle = 0
  LastAngle = 0
  MakeFace = false
  Placement = pos=(105.375,5.5,0) rot=(0,0,1;0rad)
  Radius = 1.25
FEATURE [Part::Part2DObjectPython] Circle022  # Draft 2D object (typed FeaturePython)
  FirstAngle = 0
  LastAngle = 0
  MakeFace = false
  Placement = pos=(144.625,5.5,0) rot=(0,0,1;0rad)
  Radius = 1.25
FEATURE [Part::Part2DObjectPython] Circle023  # Draft 2D object (typed FeaturePython)
  FirstAngle = 0
  LastAngle = 0
  MakeFace = false
  Placement = pos=(-2.5,5.5,0) rot=(0,0,1;0rad)
  Radius = 1.25
FEATURE [Part::Part2DObjectPython] Line295  # Draft 2D object (typed FeaturePython)
  ChamferSize = 0
  Closed = false
  End = (255,10,0)
  FilletRadius = 0
  Length = 260
  MakeFace = false
  Placement = pos=(-5,10,0) rot=(0,0,1;0rad)
  Points = (2) [(0,0,0),(260,8.88178e-15,0)]
  Start = (-5,10,0)
  Subdivisions = 0
FEATURE [Part::Part2DObjectPython] Circle024  # Draft 2D object (typed FeaturePython)
  FirstAngle = 0
  LastAngle = 0
  MakeFace = false
  Placement = pos=(125,-83.5,0) rot=(0,0,1;0rad)
  Radius = 1.25
FEATURE [App::DocumentObjectGroup] Group031  label="Outside002"
  Group = -> [Line293,Line292,Line294,Arc063,Arc056,Arc062,Arc058,Circle021,Circle022,Circle024,Circle023,Circle017,Circle020,Circle018,Line295]
FEATURE [Part::Part2DObjectPython] Line296  # Draft 2D object (typed FeaturePython)
  ChamferSize = 0
  Closed = false
  End = (248.5,0,0)
  FilletRadius = 0
  Length = 247
  MakeFace = false
  Placement = pos=(1,0,0) rot=(0,0,1;0rad)
  Points = (2) [(0.5,0,0),(247.5,0,0)]
  Start = (1.5,0,0)
  Subdivisions = 0
FEATURE [Part::Part2DObjectPython] Line297  # Draft 2D object (typed FeaturePython)
  ChamferSize = 0
  Closed = false
  End = (249.5,-1,0)
  FilletRadius = 0
  Length = 76
  MakeFace = false
  Placement = pos=(249.5,-77.5,0) rot=(0,0,1;0rad)
  Points = (2) [(0,0.5,0),(0,76.5,0)]
  Start = (249.5,-77,0)
  Subdivisions = 0
FEATURE [Part::Part2DObjectPython] Arc064  # Draft 2D object (typed FeaturePython)
  FirstAngle = 90
  LastAngle = 180
  MakeFace = false
  Placement = pos=(1.5,-1,0) rot=(0,0,1;0rad)
  Radius = 1
FEATURE [Part::Part2DObjectPython] Arc065  # Draft 2D object (typed FeaturePython)
  FirstAngle = -180
  LastAngle = -90
  MakeFace = false
  Placement = pos=(1.5,-77,0) rot=(0,0,1;0rad)
  Radius = 1
FEATURE [Part::Part2DObjectPython] Arc066  # Draft 2D object (typed FeaturePython)
  FirstAngle = 90
  LastAngle = 180
  MakeFace = false
  Placement = pos=(248.5,-77,0) rot=(0,0,1;3.14159rad)
  Radius = 1
FEATURE [Part::Part2DObjectPython] Arc067  # Draft 2D object (typed FeaturePython)
  FirstAngle = -180
  LastAngle = -90
  MakeFace = false
  Placement = pos=(248.5,-1,0) rot=(0,0,1;3.14159rad)
  Radius = 1
FEATURE [App::DocumentObjectGroup] Group030  label="Top"
  Group = -> [Line296,Line282,Line297,Arc064,Arc065,Arc066,Arc067,Arc057,Arc060,Arc061,Arc059,Line283,Line284,Line285,Line286,Line287,Line288,Line289,Line290,Line291,Group031]
FEATURE [Part::Part2DObjectPython] Line299  # Draft 2D object (typed FeaturePython)
  ChamferSize = 0
  Closed = false
  End = (131,10,0)
  FilletRadius = 0
  Length = 9
  MakeFace = false
  Placement = pos=(131,1,0) rot=(0,0,1;0rad)
  Points = (2) [(0,0,0),(0,9,0)]
  Start = (131,1,0)
  Subdivisions = 0
FEATURE [Part::Part2DObjectPython] Line300  # Draft 2D object (typed FeaturePython)
  ChamferSize = 0
  Closed = false
  End = (119,10,0)
  FilletRadius = 0
  Length = 9
  MakeFace = false
  Placement = pos=(119,1,0) rot=(0,0,1;0rad)
  Points = (2) [(0,0,0),(0,9,0)]
  Start = (119,1,0)
  Subdivisions = 0
FEATURE [Part::Part2DObjectPython] Circle025  # Draft 2D object (typed FeaturePython)
  FirstAngle = 0
  LastAngle = 0
  MakeFace = false
  Placement = pos=(252.5,5.5,0) rot=(0,0,1;0rad)
  Radius = 1.85
FEATURE [Part::Part2DObjectPython] Arc070  # Draft 2D object (typed FeaturePython)
  FirstAngle = -180
  LastAngle = -90
  MakeFace = false
  Placement = pos=(250,2.8e-14,0) rot=(0,0,1;3.14159rad)
  Radius = 1
FEATURE [Part::Part2DObjectPython] Line311  # Draft 2D object (typed FeaturePython)
  ChamferSize = 0
  Closed = false
  End = (251,0,0)
  FilletRadius = 0
  Length = 78
  MakeFace = false
  Placement = pos=(251,-79,0) rot=(0,0,1;0rad)
  Points = (2) [(1.78814e-07,1,0),(0,79,0)]
  Start = (251,-78,0)
  Subdivisions = 0
FEATURE [Part::Part2DObjectPython] Line312  # Draft 2D object (typed FeaturePython)
  ChamferSize = 0
  Closed = false
  End = (-1,0,0)
  FilletRadius = 0
  Length = 78
  MakeFace = false
  Placement = pos=(-1,-79,0) rot=(0,0,1;0rad)
  Points = (2) [(7.10543e-15,1,0),(9.54792e-15,79,0)]
  Start = (-1,-78,0)
  Subdivisions = 0
FEATURE [Part::Part2DObjectPython] Line315  # Draft 2D object (typed FeaturePython)
  ChamferSize = 0
  Closed = false
  End = (257,-86,0)
  FilletRadius = 0
  Length = 94
  MakeFace = false
  Placement = pos=(257,10,0) rot=(0,0,1;0rad)
  Points = (2) [(1.78814e-07,-2,0),(1.78814e-07,-96,0)]
  Start = (257,8,0)
  Subdivisions = 0
FEATURE [Part::Part2DObjectPython] Line316  # Draft 2D object (typed FeaturePython)
  ChamferSize = 0
  Closed = false
  End = (255,10,0)
  FilletRadius = 0
  Length = 124
  MakeFace = false
  Placement = pos=(131,10,0) rot=(0,0,1;0rad)
  Points = (2) [(0,0,0),(124,-8.88178e-15,0)]
  Start = (131,10,0)
  Subdivisions = 0
FEATURE [Part::Part2DObjectPython] Arc071  # Draft 2D object (typed FeaturePython)
  FirstAngle = -180
  LastAngle = -90
  MakeFace = false
  Placement = pos=(-5,-86,0) rot=(0,0,1;0rad)
  Radius = 2
FEATURE [Part::Part2DObjectPython] Line317  # Draft 2D object (typed FeaturePython)
  ChamferSize = 0
  Closed = false
  End = (-5,-88,0)
  FilletRadius = 0
  Length = 260
  MakeFace = false
  Placement = pos=(255,-88,0) rot=(0,0,1;0rad)
  Points = (2) [(1.78814e-07,1.42109e-14,0),(-260,1.42109e-14,0)]
  Start = (255,-88,0)
  Subdivisions = 0
FEATURE [Part::Part2DObjectPython] Line318  # Draft 2D object (typed FeaturePython)
  ChamferSize = 0
  Closed = false
  End = (-5,10,0)
  FilletRadius = 0
  Length = 124
  MakeFace = false
  Placement = pos=(119,10,0) rot=(0,0,1;0rad)
  Points = (2) [(0,-7.10543e-15,0),(-124,-7.10543e-15,0)]
  Start = (119,10,0)
  Subdivisions = 0
FEATURE [Part::Part2DObjectPython] Line319  # Draft 2D object (typed FeaturePython)
  ChamferSize = 0
  Closed = false
  End = (-7,8,0)
  FilletRadius = 0
  Length = 94
  MakeFace = false
  Placement = pos=(-7,-88,0) rot=(0,0,1;0rad)
  Points = (2) [(5.32907e-15,2,0),(5.32907e-15,96,0)]
  Start = (-7,-86,0)
  Subdivisions = 0
FEATURE [Part::Part2DObjectPython] Arc072  # Draft 2D object (typed FeaturePython)
  FirstAngle = 90
  LastAngle = 180
  MakeFace = false
  Placement = pos=(-5,8,0) rot=(0,0,1;0rad)
  Radius = 2
FEATURE [Part::Part2DObjectPython] Circle027  # Draft 2D object (typed FeaturePython)
  FirstAngle = 0
  LastAngle = 0
  MakeFace = false
  Placement = pos=(125,-83.5,0) rot=(0,0,1;0rad)
  Radius = 1.85
FEATURE [Part::Part2DObjectPython] Arc073  # Draft 2D object (typed FeaturePython)
  FirstAngle = -90
  LastAngle = 0
  MakeFace = false
  Placement = pos=(255,-86,0) rot=(0,0,1;0rad)
  Radius = 2
FEATURE [Part::Part2DObjectPython] Arc074  # Draft 2D object (typed FeaturePython)
  FirstAngle = 0
  LastAngle = 90
  MakeFace = false
  Placement = pos=(255,8,0) rot=(0,0,1;0rad)
  Radius = 2
FEATURE [Part::Part2DObjectPython] Circle028  # Draft 2D object (typed FeaturePython)
  FirstAngle = 0
  LastAngle = 0
  MakeFace = false
  Placement = pos=(105.375,5.5,0) rot=(0,0,1;0rad)
  Radius = 1.85
FEATURE [Part::Part2DObjectPython] Circle029  # Draft 2D object (typed FeaturePython)
  FirstAngle = 0
  LastAngle = 0
  MakeFace = false
  Placement = pos=(144.625,5.5,0) rot=(0,0,1;0rad)
  Radius = 1.85
FEATURE [Part::Part2DObjectPython] Circle030  # Draft 2D object (typed FeaturePython)
  FirstAngle = 0
  LastAngle = 0
  MakeFace = false
  Placement = pos=(-2.5,5.5,0) rot=(0,0,1;0rad)
  Radius = 1.85
FEATURE [Part::Part2DObjectPython] Circle031  # Draft 2D object (typed FeaturePython)
  FirstAngle = 0
  LastAngle = 0
  MakeFace = false
  Placement = pos=(-2.5,-83.5,0) rot=(0,0,1;0rad)
  Radius = 1.85
FEATURE [Part::Part2DObjectPython] Circle032  # Draft 2D object (typed FeaturePython)
  FirstAngle = 0
  LastAngle = 0
  MakeFace = false
  Placement = pos=(252.5,-83.5,0) rot=(0,0,1;0rad)
  Radius = 1.85
FEATURE [App::DocumentObjectGroup] Group032  label="Outside003"
  Group = -> [Line316,Line315,Line317,Line318,Line319,Arc072,Arc071,Arc073,Arc074,Circle028,Circle029,Circle027,Circle030,Circle031,Circle025,Circle032]
FEATURE [Part::Part2DObjectPython] Arc089  # Draft 2D object (typed FeaturePython)
  FirstAngle = 90
  LastAngle = 180
  MakeFace = false
  Placement = pos=(0,1e-16,0) rot=(0,0,1;0rad)
  Radius = 1
FEATURE [Part::Part2DObjectPython] Arc090  # Draft 2D object (typed FeaturePython)
  FirstAngle = -180
  LastAngle = -90
  MakeFace = false
  Placement = pos=(-1e-16,-78,0) rot=(0,0,1;0rad)
  Radius = 1
FEATURE [App::DocumentObjectGroup] Group041
  Group = -> [Arc089,Arc090]
FEATURE [Part::Part2DObjectPython] Arc107  # Draft 2D object (typed FeaturePython)
  FirstAngle = 90
  LastAngle = 180
  MakeFace = false
  Placement = pos=(250,-78,0) rot=(0,0,1;3.14159rad)
  Radius = 1
FEATURE [App::DocumentObjectGroup] Group042
  Group = -> [Arc107,Arc070]
FEATURE [Part::Part2DObjectPython] Line320  # Draft 2D object (typed FeaturePython)
  ChamferSize = 0
  Closed = false
  End = (119,1,0)
  FilletRadius = 0
  Length = 119
  MakeFace = false
  Placement = pos=(-1e-16,1,0) rot=(0,0,1;0rad)
  Points = (2) [(0,0,0),(119,3.77476e-15,0)]
  Start = (-1e-16,1,0)
  Subdivisions = 0
FEATURE [Part::Part2DObjectPython] Line321  # Draft 2D object (typed FeaturePython)
  ChamferSize = 0
  Closed = false
  End = (250,1,0)
  FilletRadius = 0
  Length = 119
  MakeFace = false
  Placement = pos=(131,1,0) rot=(0,0,1;0rad)
  Points = (2) [(0,0,0),(119,3.77476e-15,0)]
  Start = (131,1,0)
  Subdivisions = 0
FEATURE [Part::Part2DObjectPython] Line322  # Draft 2D object (typed FeaturePython)
  ChamferSize = 0
  Closed = false
  End = (0,-79,0)
  FilletRadius = 0
  Length = 250
  MakeFace = false
  Placement = pos=(250,-79,0) rot=(0,0,1;0rad)
  Points = (2) [(0,0,0),(-250,0,0)]
  Start = (250,-79,0)
  Subdivisions = 0
FEATURE [App::DocumentObjectGroup] Group043  label="Resting"
  Group = -> [Group042,Group041,Line311,Line312,Line300,Line299,Group032,Line320,Line321,Line322]
FEATURE [Part::Part2DObjectPython] Line325  # Draft 2D object (typed FeaturePython)
  ChamferSize = 0
  Closed = false
  End = (131,10,0)
  FilletRadius = 0
  Length = 15
  MakeFace = false
  Placement = pos=(131,1,0) rot=(0,0,1;0rad)
  Points = (2) [(0,-6,0),(0,9,0)]
  Start = (131,-5,0)
  Subdivisions = 0
FEATURE [Part::Part2DObjectPython] Arc108  # Draft 2D object (typed FeaturePython)
  FirstAngle = -180
  LastAngle = -90
  MakeFace = false
  Placement = pos=(-5,-86,0) rot=(0,0,1;0rad)
  Radius = 2
FEATURE [Part::Part2DObjectPython] Line326  # Draft 2D object (typed FeaturePython)
  ChamferSize = 0
  Closed = false
  End = (-5,-88,0)
  FilletRadius = 0
  Length = 260
  MakeFace = false
  Placement = pos=(255,-88,0) rot=(0,0,1;0rad)
  Points = (2) [(1.78814e-07,1.42109e-14,0),(-260,1.42109e-14,0)]
  Start = (255,-88,0)
  Subdivisions = 0
FEATURE [Part::Part2DObjectPython] Line327  # Draft 2D object (typed FeaturePython)
  ChamferSize = 0
  Closed = false
  End = (-5,10,0)
  FilletRadius = 0
  Length = 124
  MakeFace = false
  Placement = pos=(119,10,0) rot=(0,0,1;0rad)
  Points = (2) [(0,-7.10543e-15,0),(-124,-7.10543e-15,0)]
  Start = (119,10,0)
  Subdivisions = 0
FEATURE [Part::Part2DObjectPython] Line328  # Draft 2D object (typed FeaturePython)
  ChamferSize = 0
  Closed = false
  End = (-7,8,0)
  FilletRadius = 0
  Length = 94
  MakeFace = false
  Placement = pos=(-7,-88,0) rot=(0,0,1;0rad)
  Points = (2) [(5.32907e-15,2,0),(5.32907e-15,96,0)]
  Start = (-7,-86,0)
  Subdivisions = 0
FEATURE [Part::Part2DObjectPython] Arc109  # Draft 2D object (typed FeaturePython)
  FirstAngle = 90
  LastAngle = 180
  MakeFace = false
  Placement = pos=(-5,8,0) rot=(0,0,1;0rad)
  Radius = 2
FEATURE [Part::Part2DObjectPython] Line329  # Draft 2D object (typed FeaturePython)
  ChamferSize = 0
  Closed = false
  End = (119,10,0)
  FilletRadius = 0
  Length = 15
  MakeFace = false
  Placement = pos=(119,1,0) rot=(0,0,1;0rad)
  Points = (2) [(0,-6,0),(0,9,0)]
  Start = (119,-5,0)
  Subdivisions = 0
FEATURE [Part::Part2DObjectPython] Circle034  # Draft 2D object (typed FeaturePython)
  FirstAngle = 0
  LastAngle = 0
  MakeFace = false
  Placement = pos=(125,-83.5,0) rot=(0,0,1;0rad)
  Radius = 1.25
FEATURE [Part::Part2DObjectPython] Arc111  # Draft 2D object (typed FeaturePython)
  FirstAngle = -90
  LastAngle = 0
  MakeFace = false
  Placement = pos=(255,-86,0) rot=(0,0,1;0rad)
  Radius = 2
FEATURE [Part::Part2DObjectPython] Arc112  # Draft 2D object (typed FeaturePython)
  FirstAngle = 0
  LastAngle = 90
  MakeFace = false
  Placement = pos=(255,8,0) rot=(0,0,1;0rad)
  Radius = 2
FEATURE [Part::Part2DObjectPython] Circle035  # Draft 2D object (typed FeaturePython)
  FirstAngle = 0
  LastAngle = 0
  MakeFace = false
  Placement = pos=(105.375,5.5,0) rot=(0,0,1;0rad)
  Radius = 1.25
FEATURE [Part::Part2DObjectPython] Circle036  # Draft 2D object (typed FeaturePython)
  FirstAngle = 0
  LastAngle = 0
  MakeFace = false
  Placement = pos=(144.625,5.5,0) rot=(0,0,1;0rad)
  Radius = 1.25
FEATURE [Part::Part2DObjectPython] Circle037  # Draft 2D object (typed FeaturePython)
  FirstAngle = 0
  LastAngle = 0
  MakeFace = false
  Placement = pos=(-2.5,5.5,0) rot=(0,0,1;0rad)
  Radius = 1.25
FEATURE [Part::Part2DObjectPython] Circle038  # Draft 2D object (typed FeaturePython)
  FirstAngle = 0
  LastAngle = 0
  MakeFace = false
  Placement = pos=(252.5,5.5,0) rot=(0,0,1;0rad)
  Radius = 1.25
FEATURE [Part::Part2DObjectPython] Line330  # Draft 2D object (typed FeaturePython)
  ChamferSize = 0
  Closed = false
  End = (257,-86,0)
  FilletRadius = 0
  Length = 94
  MakeFace = false
  Placement = pos=(257,10,0) rot=(0,0,1;0rad)
  Points = (2) [(1.78814e-07,-2,0),(1.78814e-07,-96,0)]
  Start = (257,8,0)
  Subdivisions = 0
FEATURE [Part::Part2DObjectPython] Line331  # Draft 2D object (typed FeaturePython)
  ChamferSize = 0
  Closed = false
  End = (255,10,0)
  FilletRadius = 0
  Length = 124
  MakeFace = false
  Placement = pos=(131,10,0) rot=(0,0,1;0rad)
  Points = (2) [(0,0,0),(124,-8.88178e-15,0)]
  Start = (131,10,0)
  Subdivisions = 0
FEATURE [Part::Part2DObjectPython] Circle039  # Draft 2D object (typed FeaturePython)
  FirstAngle = 0
  LastAngle = 0
  MakeFace = false
  Placement = pos=(-2.5,-83.5,0) rot=(0,0,1;0rad)
  Radius = 1.25
FEATURE [Part::Part2DObjectPython] Circle040  # Draft 2D object (typed FeaturePython)
  FirstAngle = 0
  LastAngle = 0
  MakeFace = false
  Placement = pos=(252.5,-83.5,0) rot=(0,0,1;0rad)
  Radius = 1.25
FEATURE [App::DocumentObjectGroup] Group047  label="Outside004"
  Group = -> [Line331,Line330,Line326,Line327,Line328,Arc109,Arc108,Arc111,Arc112,Circle035,Circle036,Circle034,Circle037,Circle039,Circle038,Circle040]
FEATURE [Part::Part2DObjectPython] Line332  # Draft 2D object (typed FeaturePython)
  ChamferSize = 0
  Closed = false
  End = (131,-5,0)
  FilletRadius = 0
  Length = 12
  MakeFace = false
  Placement = pos=(119,-5,0) rot=(0,0,1;0rad)
  Points = (2) [(0,0,0),(12,-2.66454e-15,0)]
  Start = (119,-5,0)
  Subdivisions = 0
FEATURE [App::DocumentObjectGroup] Group044  label="Bottom"
  Group = -> [Line329,Line325,Group047,Line332]
